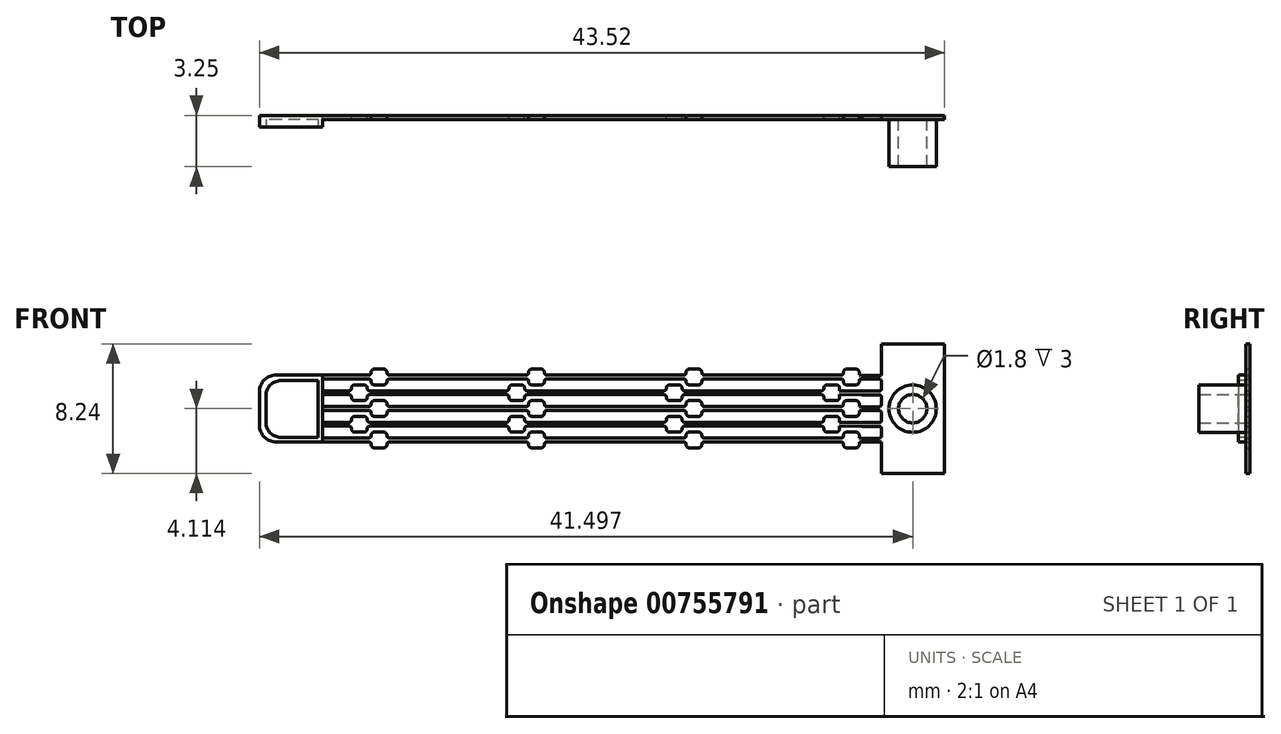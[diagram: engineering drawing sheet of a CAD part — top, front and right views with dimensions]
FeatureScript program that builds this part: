
annotation { "Feature Type Name" : "Feature", "Feature Type Description" : "" }
export const myFeature = defineFeature(function(context is Context, id is Id, definition is map)
    precondition{}
    {
        {
            var Q0;
            Q0=qCreatedBy(makeId("Front.planeOp"),FACE);
            var sketch = newSketch(context, id + "F0", { "sketchPlane" : qUnion([Q0])});
            skLineSegment(sketch, "E0.0.5.4", {"start": v(50.52, 28.02) * mm, "end": v(49.92, 28.02) * mm});
            skLineSegment(sketch, "E0.0.5.5", {"start": v(50.52, 27.02) * mm, "end": v(49.92, 27.02) * mm});
            skLineSegment(sketch, "E0.0.5.6", {"start": v(49.57, 27.4) * mm, "end": v(49.13, 27.4) * mm});
            skLineSegment(sketch, "E0.0.5.7", {"start": v(49.57, 27.64) * mm, "end": v(49.13, 27.64) * mm});
            skPoint(sketch, "E0.0.5.9", {"position": v(49.72, 27.64) * mm});
            skPoint(sketch, "E0.0.5.10", {"position": v(49.72, 28.02) * mm});
            skPoint(sketch, "E0.0.5.11", {"position": v(50.72, 27.4) * mm});
            skPoint(sketch, "E0.0.5.12", {"position": v(50.72, 28.02) * mm});
            skPoint(sketch, "E0.0.5.13", {"position": v(50.72, 27.64) * mm});
            skPoint(sketch, "E0.0.5.15", {"position": v(50.22, 27.52) * mm});
            skLineSegment(sketch, "E0.0.5.18", {"start": v(49.13, 27.4) * mm, "end": v(47.89, 27.4) * mm});
            skLineSegment(sketch, "E0.0.5.19", {"start": v(49.13, 27.64) * mm, "end": v(47.89, 27.64) * mm});
            skPoint(sketch, "E0.0.5.29", {"position": v(49.72, 27.4) * mm});
            skPoint(sketch, "E0.0.5.31", {"position": v(50.22, 27.52) * mm});
            skLineSegment(sketch, "E0.0.5.32", {"start": v(51.17, 27.4) * mm, "end": v(50.87, 27.4) * mm});
            skLineSegment(sketch, "E0.0.5.33", {"start": v(51.17, 27.64) * mm, "end": v(50.87, 27.64) * mm});
            skArc(sketch, "E0.0.5.34", {"start": v(50.72, 27.8) * mm, "mid": v(50.77, 27.69) * mm, "end": v(50.87, 27.64) * mm});
            skArc(sketch, "E0.0.5.41", {"start": v(50.52, 27.02) * mm, "mid": v(50.66, 27.08) * mm, "end": v(50.72, 27.22) * mm});
            skArc(sketch, "E0.0.5.44", {"start": v(49.72, 27.22) * mm, "mid": v(49.78, 27.08) * mm, "end": v(49.92, 27.02) * mm});
            skArc(sketch, "E0.0.5.45", {"start": v(49.92, 28.02) * mm, "mid": v(49.78, 27.96) * mm, "end": v(49.72, 27.82) * mm});
            skArc(sketch, "E0.0.5.46", {"start": v(50.72, 27.82) * mm, "mid": v(50.66, 27.96) * mm, "end": v(50.52, 28.02) * mm});
            skLineSegment(sketch, "E0.0.5.49", {"start": v(49.72, 27.22) * mm, "end": v(49.72, 27.24) * mm});
            skLineSegment(sketch, "E0.0.5.50", {"start": v(50.72, 27.22) * mm, "end": v(50.72, 27.24) * mm});
            skArc(sketch, "E0.0.5.55", {"start": v(49.72, 27.24) * mm, "mid": v(49.68, 27.35) * mm, "end": v(49.57, 27.4) * mm});
            skArc(sketch, "E0.0.5.56", {"start": v(50.87, 27.4) * mm, "mid": v(50.77, 27.35) * mm, "end": v(50.72, 27.24) * mm});
            skLineSegment(sketch, "E0.0.5.57", {"start": v(49.72, 27.8) * mm, "end": v(49.72, 27.82) * mm});
            skLineSegment(sketch, "E0.0.5.60", {"start": v(50.72, 27.8) * mm, "end": v(50.72, 27.82) * mm});
            skArc(sketch, "E0.0.5.61", {"start": v(49.57, 27.64) * mm, "mid": v(49.68, 27.69) * mm, "end": v(49.72, 27.8) * mm});
            skLineSegment(sketch, "E0.0.6.0", {"start": v(47.89, 28.4) * mm, "end": v(48.32, 28.4) * mm});
            skLineSegment(sketch, "E0.0.6.1", {"start": v(47.89, 28.64) * mm, "end": v(48.32, 28.64) * mm});
            skLineSegment(sketch, "E0.0.6.2", {"start": v(49.27, 29.02) * mm, "end": v(48.67, 29.02) * mm});
            skLineSegment(sketch, "E0.0.6.3", {"start": v(49.27, 28.02) * mm, "end": v(48.67, 28.02) * mm});
            skLineSegment(sketch, "E0.0.6.4", {"start": v(50.52, 30.02) * mm, "end": v(49.92, 30.02) * mm});
            skLineSegment(sketch, "E0.0.6.5", {"start": v(50.52, 29.02) * mm, "end": v(49.92, 29.02) * mm});
            skLineSegment(sketch, "E0.0.6.6", {"start": v(49.57, 29.4) * mm, "end": v(49.13, 29.4) * mm});
            skLineSegment(sketch, "E0.0.6.7", {"start": v(49.57, 29.64) * mm, "end": v(49.13, 29.64) * mm});
            skPoint(sketch, "E0.0.6.8", {"position": v(49.72, 29.02) * mm});
            skPoint(sketch, "E0.0.6.9", {"position": v(49.72, 29.64) * mm});
            skPoint(sketch, "E0.0.6.10", {"position": v(49.72, 30.02) * mm});
            skPoint(sketch, "E0.0.6.11", {"position": v(50.72, 29.4) * mm});
            skPoint(sketch, "E0.0.6.12", {"position": v(50.72, 30.02) * mm});
            skPoint(sketch, "E0.0.6.13", {"position": v(50.72, 29.64) * mm});
            skPoint(sketch, "E0.0.6.14", {"position": v(48.97, 28.52) * mm});
            skPoint(sketch, "E0.0.6.15", {"position": v(50.22, 29.52) * mm});
            skPoint(sketch, "E0.0.6.16", {"position": v(49.47, 28.02) * mm});
            skPoint(sketch, "E0.0.6.17", {"position": v(48.47, 28.4) * mm});
            skLineSegment(sketch, "E0.0.6.18", {"start": v(49.13, 29.4) * mm, "end": v(47.89, 29.4) * mm});
            skLineSegment(sketch, "E0.0.6.19", {"start": v(49.13, 29.64) * mm, "end": v(47.89, 29.64) * mm});
            skPoint(sketch, "E0.0.6.20", {"position": v(48.47, 28.02) * mm});
            skPoint(sketch, "E0.0.6.21", {"position": v(48.47, 28.64) * mm});
            skLineSegment(sketch, "E0.0.6.22", {"start": v(49.62, 28.4) * mm, "end": v(51.17, 28.4) * mm});
            skPoint(sketch, "E0.0.6.23", {"position": v(48.47, 29.02) * mm});
            skPoint(sketch, "E0.0.6.24", {"position": v(49.47, 28.4) * mm});
            skLineSegment(sketch, "E0.0.6.25", {"start": v(49.62, 28.64) * mm, "end": v(51.17, 28.64) * mm});
            skPoint(sketch, "E0.0.6.26", {"position": v(49.47, 29.02) * mm});
            skPoint(sketch, "E0.0.6.27", {"position": v(49.47, 28.64) * mm});
            skPoint(sketch, "E0.0.6.28", {"position": v(50.72, 29.02) * mm});
            skPoint(sketch, "E0.0.6.29", {"position": v(49.72, 29.4) * mm});
            skPoint(sketch, "E0.0.6.30", {"position": v(48.97, 28.52) * mm});
            skPoint(sketch, "E0.0.6.31", {"position": v(50.22, 29.52) * mm});
            skLineSegment(sketch, "E0.0.6.32", {"start": v(51.17, 29.4) * mm, "end": v(50.87, 29.4) * mm});
            skLineSegment(sketch, "E0.0.6.33", {"start": v(51.17, 29.64) * mm, "end": v(50.87, 29.64) * mm});
            skArc(sketch, "E0.0.6.34", {"start": v(50.72, 29.8) * mm, "mid": v(50.77, 29.69) * mm, "end": v(50.87, 29.64) * mm});
            skArc(sketch, "E0.0.6.35", {"start": v(49.27, 28.02) * mm, "mid": v(49.41, 28.08) * mm, "end": v(49.47, 28.22) * mm});
            skArc(sketch, "E0.0.6.36", {"start": v(48.47, 28.22) * mm, "mid": v(48.53, 28.08) * mm, "end": v(48.67, 28.02) * mm});
            skArc(sketch, "E0.0.6.37", {"start": v(48.67, 29.02) * mm, "mid": v(48.53, 28.96) * mm, "end": v(48.47, 28.82) * mm});
            skArc(sketch, "E0.0.6.39", {"start": v(49.47, 28.82) * mm, "mid": v(49.41, 28.96) * mm, "end": v(49.27, 29.02) * mm});
            skArc(sketch, "E0.0.6.41", {"start": v(50.52, 29.02) * mm, "mid": v(50.66, 29.08) * mm, "end": v(50.72, 29.22) * mm});
            skArc(sketch, "E0.0.6.44", {"start": v(49.72, 29.22) * mm, "mid": v(49.78, 29.08) * mm, "end": v(49.92, 29.02) * mm});
            skArc(sketch, "E0.0.6.45", {"start": v(49.92, 30.02) * mm, "mid": v(49.78, 29.96) * mm, "end": v(49.72, 29.82) * mm});
            skArc(sketch, "E0.0.6.46", {"start": v(50.72, 29.82) * mm, "mid": v(50.66, 29.96) * mm, "end": v(50.52, 30.02) * mm});
            skArc(sketch, "E0.0.6.47", {"start": v(48.47, 28.24) * mm, "mid": v(48.43, 28.35) * mm, "end": v(48.32, 28.4) * mm});
            skArc(sketch, "E0.0.6.48", {"start": v(49.62, 28.4) * mm, "mid": v(49.52, 28.35) * mm, "end": v(49.47, 28.24) * mm});
            skLineSegment(sketch, "E0.0.6.49", {"start": v(49.72, 29.22) * mm, "end": v(49.72, 29.24) * mm});
            skLineSegment(sketch, "E0.0.6.50", {"start": v(50.72, 29.22) * mm, "end": v(50.72, 29.24) * mm});
            skArc(sketch, "E0.0.6.51", {"start": v(48.32, 28.64) * mm, "mid": v(48.43, 28.69) * mm, "end": v(48.47, 28.8) * mm});
            skLineSegment(sketch, "E0.0.6.52", {"start": v(48.47, 28.8) * mm, "end": v(48.47, 28.82) * mm});
            skArc(sketch, "E0.0.6.53", {"start": v(49.47, 28.8) * mm, "mid": v(49.52, 28.69) * mm, "end": v(49.62, 28.64) * mm});
            skLineSegment(sketch, "E0.0.6.54", {"start": v(49.47, 28.8) * mm, "end": v(49.47, 28.82) * mm});
            skArc(sketch, "E0.0.6.55", {"start": v(49.72, 29.24) * mm, "mid": v(49.68, 29.35) * mm, "end": v(49.57, 29.4) * mm});
            skArc(sketch, "E0.0.6.56", {"start": v(50.87, 29.4) * mm, "mid": v(50.77, 29.35) * mm, "end": v(50.72, 29.24) * mm});
            skLineSegment(sketch, "E0.0.6.57", {"start": v(49.72, 29.8) * mm, "end": v(49.72, 29.82) * mm});
            skLineSegment(sketch, "E0.0.6.58", {"start": v(48.47, 28.22) * mm, "end": v(48.47, 28.24) * mm});
            skLineSegment(sketch, "E0.0.6.59", {"start": v(49.47, 28.22) * mm, "end": v(49.47, 28.24) * mm});
            skLineSegment(sketch, "E0.0.6.60", {"start": v(50.72, 29.8) * mm, "end": v(50.72, 29.82) * mm});
            skArc(sketch, "E0.0.6.61", {"start": v(49.57, 29.64) * mm, "mid": v(49.68, 29.69) * mm, "end": v(49.72, 29.8) * mm});
            skLineSegment(sketch, "E0.0.7.0", {"start": v(47.89, 30.4) * mm, "end": v(48.32, 30.4) * mm});
            skLineSegment(sketch, "E0.0.7.1", {"start": v(47.89, 30.64) * mm, "end": v(48.32, 30.64) * mm});
            skLineSegment(sketch, "E0.0.7.2", {"start": v(49.27, 31.02) * mm, "end": v(48.67, 31.02) * mm});
            skLineSegment(sketch, "E0.0.7.3", {"start": v(49.27, 30.02) * mm, "end": v(48.67, 30.02) * mm});
            skLineSegment(sketch, "E0.0.7.4", {"start": v(50.52, 32.02) * mm, "end": v(49.92, 32.02) * mm});
            skLineSegment(sketch, "E0.0.7.5", {"start": v(50.52, 31.02) * mm, "end": v(49.92, 31.02) * mm});
            skLineSegment(sketch, "E0.0.7.6", {"start": v(49.57, 31.4) * mm, "end": v(49.13, 31.4) * mm});
            skLineSegment(sketch, "E0.0.7.7", {"start": v(49.57, 31.64) * mm, "end": v(49.13, 31.64) * mm});
            skPoint(sketch, "E0.0.7.8", {"position": v(49.72, 31.02) * mm});
            skPoint(sketch, "E0.0.7.9", {"position": v(49.72, 31.64) * mm});
            skPoint(sketch, "E0.0.7.10", {"position": v(49.72, 32.02) * mm});
            skPoint(sketch, "E0.0.7.11", {"position": v(50.72, 31.4) * mm});
            skPoint(sketch, "E0.0.7.12", {"position": v(50.72, 32.02) * mm});
            skPoint(sketch, "E0.0.7.13", {"position": v(50.72, 31.64) * mm});
            skPoint(sketch, "E0.0.7.14", {"position": v(48.97, 30.52) * mm});
            skPoint(sketch, "E0.0.7.15", {"position": v(50.22, 31.52) * mm});
            skPoint(sketch, "E0.0.7.16", {"position": v(49.47, 30.02) * mm});
            skPoint(sketch, "E0.0.7.17", {"position": v(48.47, 30.4) * mm});
            skLineSegment(sketch, "E0.0.7.18", {"start": v(49.13, 31.4) * mm, "end": v(47.89, 31.4) * mm});
            skLineSegment(sketch, "E0.0.7.19", {"start": v(49.13, 31.64) * mm, "end": v(47.89, 31.64) * mm});
            skPoint(sketch, "E0.0.7.20", {"position": v(48.47, 30.02) * mm});
            skPoint(sketch, "E0.0.7.21", {"position": v(48.47, 30.64) * mm});
            skLineSegment(sketch, "E0.0.7.22", {"start": v(49.62, 30.4) * mm, "end": v(51.17, 30.4) * mm});
            skPoint(sketch, "E0.0.7.23", {"position": v(48.47, 31.02) * mm});
            skPoint(sketch, "E0.0.7.24", {"position": v(49.47, 30.4) * mm});
            skLineSegment(sketch, "E0.0.7.25", {"start": v(49.62, 30.64) * mm, "end": v(51.17, 30.64) * mm});
            skPoint(sketch, "E0.0.7.26", {"position": v(49.47, 31.02) * mm});
            skPoint(sketch, "E0.0.7.27", {"position": v(49.47, 30.64) * mm});
            skPoint(sketch, "E0.0.7.28", {"position": v(50.72, 31.02) * mm});
            skPoint(sketch, "E0.0.7.29", {"position": v(49.72, 31.4) * mm});
            skPoint(sketch, "E0.0.7.30", {"position": v(48.97, 30.52) * mm});
            skPoint(sketch, "E0.0.7.31", {"position": v(50.22, 31.52) * mm});
            skLineSegment(sketch, "E0.0.7.32", {"start": v(51.17, 31.4) * mm, "end": v(50.87, 31.4) * mm});
            skLineSegment(sketch, "E0.0.7.33", {"start": v(51.17, 31.64) * mm, "end": v(50.87, 31.64) * mm});
            skArc(sketch, "E0.0.7.34", {"start": v(50.72, 31.8) * mm, "mid": v(50.77, 31.69) * mm, "end": v(50.87, 31.64) * mm});
            skArc(sketch, "E0.0.7.35", {"start": v(49.27, 30.02) * mm, "mid": v(49.41, 30.08) * mm, "end": v(49.47, 30.22) * mm});
            skArc(sketch, "E0.0.7.36", {"start": v(48.47, 30.22) * mm, "mid": v(48.53, 30.08) * mm, "end": v(48.67, 30.02) * mm});
            skArc(sketch, "E0.0.7.37", {"start": v(48.67, 31.02) * mm, "mid": v(48.53, 30.96) * mm, "end": v(48.47, 30.82) * mm});
            skArc(sketch, "E0.0.7.39", {"start": v(49.47, 30.82) * mm, "mid": v(49.41, 30.96) * mm, "end": v(49.27, 31.02) * mm});
            skArc(sketch, "E0.0.7.41", {"start": v(50.52, 31.02) * mm, "mid": v(50.66, 31.08) * mm, "end": v(50.72, 31.22) * mm});
            skArc(sketch, "E0.0.7.44", {"start": v(49.72, 31.22) * mm, "mid": v(49.78, 31.08) * mm, "end": v(49.92, 31.02) * mm});
            skArc(sketch, "E0.0.7.45", {"start": v(49.92, 32.02) * mm, "mid": v(49.78, 31.96) * mm, "end": v(49.72, 31.82) * mm});
            skArc(sketch, "E0.0.7.46", {"start": v(50.72, 31.82) * mm, "mid": v(50.66, 31.96) * mm, "end": v(50.52, 32.02) * mm});
            skArc(sketch, "E0.0.7.47", {"start": v(48.47, 30.24) * mm, "mid": v(48.43, 30.35) * mm, "end": v(48.32, 30.4) * mm});
            skArc(sketch, "E0.0.7.48", {"start": v(49.62, 30.4) * mm, "mid": v(49.52, 30.35) * mm, "end": v(49.47, 30.24) * mm});
            skLineSegment(sketch, "E0.0.7.49", {"start": v(49.72, 31.22) * mm, "end": v(49.72, 31.24) * mm});
            skLineSegment(sketch, "E0.0.7.50", {"start": v(50.72, 31.22) * mm, "end": v(50.72, 31.24) * mm});
            skArc(sketch, "E0.0.7.51", {"start": v(48.32, 30.64) * mm, "mid": v(48.43, 30.69) * mm, "end": v(48.47, 30.8) * mm});
            skLineSegment(sketch, "E0.0.7.52", {"start": v(48.47, 30.8) * mm, "end": v(48.47, 30.82) * mm});
            skArc(sketch, "E0.0.7.53", {"start": v(49.47, 30.8) * mm, "mid": v(49.52, 30.69) * mm, "end": v(49.62, 30.64) * mm});
            skLineSegment(sketch, "E0.0.7.54", {"start": v(49.47, 30.8) * mm, "end": v(49.47, 30.82) * mm});
            skArc(sketch, "E0.0.7.55", {"start": v(49.72, 31.24) * mm, "mid": v(49.68, 31.35) * mm, "end": v(49.57, 31.4) * mm});
            skArc(sketch, "E0.0.7.56", {"start": v(50.87, 31.4) * mm, "mid": v(50.77, 31.35) * mm, "end": v(50.72, 31.24) * mm});
            skLineSegment(sketch, "E0.0.7.57", {"start": v(49.72, 31.8) * mm, "end": v(49.72, 31.82) * mm});
            skLineSegment(sketch, "E0.0.7.58", {"start": v(48.47, 30.22) * mm, "end": v(48.47, 30.24) * mm});
            skLineSegment(sketch, "E0.0.7.59", {"start": v(49.47, 30.22) * mm, "end": v(49.47, 30.24) * mm});
            skLineSegment(sketch, "E0.0.7.60", {"start": v(50.72, 31.8) * mm, "end": v(50.72, 31.82) * mm});
            skArc(sketch, "E0.0.7.61", {"start": v(49.57, 31.64) * mm, "mid": v(49.68, 31.69) * mm, "end": v(49.72, 31.8) * mm});
            skPoint(sketch, "E1.1.0.2", {"position": v(59.72, 32.02) * mm});
            skPoint(sketch, "E1.1.0.3", {"position": v(60.72, 32.02) * mm});
            skPoint(sketch, "E1.1.0.6", {"position": v(60.72, 31.64) * mm});
            skPoint(sketch, "E1.1.0.8", {"position": v(58.47, 28.02) * mm});
            skPoint(sketch, "E1.1.0.11", {"position": v(60.22, 31.52) * mm});
            skPoint(sketch, "E1.1.0.14", {"position": v(59.47, 30.02) * mm});
            skPoint(sketch, "E1.1.0.15", {"position": v(58.47, 29.02) * mm});
            skPoint(sketch, "E1.1.0.17", {"position": v(59.72, 28.02) * mm});
            skPoint(sketch, "E1.1.0.20", {"position": v(58.47, 30.02) * mm});
            skPoint(sketch, "E1.1.0.21", {"position": v(60.72, 27.4) * mm});
            skPoint(sketch, "E1.1.0.22", {"position": v(58.47, 30.64) * mm});
            skPoint(sketch, "E1.1.0.32", {"position": v(60.72, 29.02) * mm});
            skPoint(sketch, "E1.1.0.33", {"position": v(58.47, 31.02) * mm});
            skPoint(sketch, "E1.1.0.34", {"position": v(60.72, 28.02) * mm});
            skPoint(sketch, "E1.1.0.35", {"position": v(59.72, 29.02) * mm});
            skPoint(sketch, "E1.1.0.38", {"position": v(59.72, 31.64) * mm});
            skPoint(sketch, "E1.1.0.39", {"position": v(60.72, 29.64) * mm});
            skPoint(sketch, "E1.1.0.43", {"position": v(60.22, 31.52) * mm});
            skPoint(sketch, "E1.1.0.44", {"position": v(60.72, 31.4) * mm});
            skPoint(sketch, "E1.1.0.49", {"position": v(58.47, 28.4) * mm});
            skPoint(sketch, "E1.1.0.52", {"position": v(58.97, 30.52) * mm});
            skPoint(sketch, "E1.1.0.57", {"position": v(58.47, 28.64) * mm});
            skPoint(sketch, "E1.1.0.67", {"position": v(59.72, 27.64) * mm});
            skPoint(sketch, "E1.1.0.68", {"position": v(58.47, 30.4) * mm});
            skPoint(sketch, "E1.1.0.69", {"position": v(59.47, 28.4) * mm});
            skPoint(sketch, "E1.1.0.71", {"position": v(60.22, 27.52) * mm});
            skPoint(sketch, "E1.1.0.72", {"position": v(59.47, 28.64) * mm});
            skPoint(sketch, "E1.1.0.78", {"position": v(59.72, 31.4) * mm});
            skPoint(sketch, "E1.1.0.80", {"position": v(60.72, 30.02) * mm});
            skPoint(sketch, "E1.1.0.82", {"position": v(60.22, 27.52) * mm});
            skPoint(sketch, "E1.1.0.83", {"position": v(60.72, 29.4) * mm});
            skPoint(sketch, "E1.1.0.85", {"position": v(60.72, 31.02) * mm});
            skPoint(sketch, "E1.1.0.88", {"position": v(58.97, 28.52) * mm});
            skPoint(sketch, "E1.1.0.90", {"position": v(58.97, 30.52) * mm});
            skPoint(sketch, "E1.1.0.92", {"position": v(60.22, 29.52) * mm});
            skPoint(sketch, "E1.1.0.94", {"position": v(60.72, 27.64) * mm});
            skPoint(sketch, "E1.1.0.106", {"position": v(59.72, 27.4) * mm});
            skPoint(sketch, "E1.1.0.110", {"position": v(59.47, 29.02) * mm});
            skPoint(sketch, "E1.1.0.113", {"position": v(60.22, 29.52) * mm});
            skPoint(sketch, "E1.1.0.117", {"position": v(59.72, 31.02) * mm});
            skPoint(sketch, "E1.1.0.126", {"position": v(59.47, 28.02) * mm});
            skPoint(sketch, "E1.1.0.134", {"position": v(58.97, 28.52) * mm});
            skPoint(sketch, "E1.1.0.141", {"position": v(59.47, 30.64) * mm});
            skPoint(sketch, "E1.1.0.147", {"position": v(59.72, 30.02) * mm});
            skPoint(sketch, "E1.1.0.148", {"position": v(59.47, 31.02) * mm});
            skPoint(sketch, "E1.1.0.154", {"position": v(59.47, 30.4) * mm});
            skPoint(sketch, "E1.1.0.155", {"position": v(59.72, 29.4) * mm});
            skPoint(sketch, "E1.1.0.156", {"position": v(59.72, 29.64) * mm});
            skLineSegment(sketch, "E1.1.0.161", {"start": v(59.13, 31.64) * mm, "end": v(57.89, 31.64) * mm});
            skLineSegment(sketch, "E1.1.0.162", {"start": v(59.13, 31.4) * mm, "end": v(57.89, 31.4) * mm});
            skLineSegment(sketch, "E1.1.0.163", {"start": v(57.89, 30.64) * mm, "end": v(58.32, 30.64) * mm});
            skLineSegment(sketch, "E1.1.0.166", {"start": v(57.89, 30.4) * mm, "end": v(58.32, 30.4) * mm});
            skLineSegment(sketch, "E1.1.0.171", {"start": v(59.13, 29.64) * mm, "end": v(57.89, 29.64) * mm});
            skLineSegment(sketch, "E1.1.0.173", {"start": v(59.13, 29.4) * mm, "end": v(57.89, 29.4) * mm});
            skLineSegment(sketch, "E1.1.0.174", {"start": v(59.13, 27.64) * mm, "end": v(57.89, 27.64) * mm});
            skArc(sketch, "E1.1.0.175", {"start": v(58.47, 28.22) * mm, "mid": v(58.53, 28.08) * mm, "end": v(58.67, 28.02) * mm});
            skLineSegment(sketch, "E1.1.0.176", {"start": v(57.89, 28.4) * mm, "end": v(58.32, 28.4) * mm});
            skLineSegment(sketch, "E1.1.0.177", {"start": v(57.89, 28.64) * mm, "end": v(58.32, 28.64) * mm});
            skLineSegment(sketch, "E1.1.0.180", {"start": v(60.52, 32.02) * mm, "end": v(59.92, 32.02) * mm});
            skLineSegment(sketch, "E1.1.0.185", {"start": v(61.17, 31.64) * mm, "end": v(60.87, 31.64) * mm});
            skLineSegment(sketch, "E1.1.0.194", {"start": v(59.13, 27.4) * mm, "end": v(57.89, 27.4) * mm});
            skLineSegment(sketch, "E1.1.0.205", {"start": v(61.17, 31.4) * mm, "end": v(60.87, 31.4) * mm});
            skArc(sketch, "E1.1.0.215", {"start": v(59.57, 31.64) * mm, "mid": v(59.68, 31.69) * mm, "end": v(59.72, 31.8) * mm});
            skArc(sketch, "E1.1.0.216", {"start": v(60.72, 31.82) * mm, "mid": v(60.66, 31.96) * mm, "end": v(60.52, 32.02) * mm});
            skArc(sketch, "E1.1.0.218", {"start": v(60.72, 31.8) * mm, "mid": v(60.77, 31.69) * mm, "end": v(60.87, 31.64) * mm});
            skLineSegment(sketch, "E1.1.0.222", {"start": v(61.17, 29.64) * mm, "end": v(60.87, 29.64) * mm});
            skLineSegment(sketch, "E1.1.0.228", {"start": v(59.72, 31.8) * mm, "end": v(59.72, 31.82) * mm});
            skLineSegment(sketch, "E1.1.0.229", {"start": v(60.72, 31.8) * mm, "end": v(60.72, 31.82) * mm});
            skLineSegment(sketch, "E1.1.0.230", {"start": v(59.62, 30.64) * mm, "end": v(61.17, 30.64) * mm});
            skArc(sketch, "E1.1.0.231", {"start": v(59.92, 32.02) * mm, "mid": v(59.78, 31.96) * mm, "end": v(59.72, 31.82) * mm});
            skLineSegment(sketch, "E1.1.0.239", {"start": v(59.27, 31.02) * mm, "end": v(58.67, 31.02) * mm});
            skLineSegment(sketch, "E1.1.0.240", {"start": v(61.17, 29.4) * mm, "end": v(60.87, 29.4) * mm});
            skLineSegment(sketch, "E1.1.0.242", {"start": v(59.57, 31.64) * mm, "end": v(59.13, 31.64) * mm});
            skArc(sketch, "E1.1.0.243", {"start": v(59.47, 30.82) * mm, "mid": v(59.41, 30.96) * mm, "end": v(59.27, 31.02) * mm});
            skArc(sketch, "E1.1.0.244", {"start": v(59.72, 31.24) * mm, "mid": v(59.68, 31.35) * mm, "end": v(59.57, 31.4) * mm});
            skArc(sketch, "E1.1.0.246", {"start": v(60.87, 31.4) * mm, "mid": v(60.77, 31.35) * mm, "end": v(60.72, 31.24) * mm});
            skLineSegment(sketch, "E1.1.0.249", {"start": v(59.57, 31.4) * mm, "end": v(59.13, 31.4) * mm});
            skLineSegment(sketch, "E1.1.0.250", {"start": v(60.52, 31.02) * mm, "end": v(59.92, 31.02) * mm});
            skArc(sketch, "E1.1.0.251", {"start": v(60.52, 31.02) * mm, "mid": v(60.66, 31.08) * mm, "end": v(60.72, 31.22) * mm});
            skLineSegment(sketch, "E1.1.0.253", {"start": v(59.62, 30.4) * mm, "end": v(61.17, 30.4) * mm});
            skLineSegment(sketch, "E1.1.0.257", {"start": v(59.72, 31.22) * mm, "end": v(59.72, 31.24) * mm});
            skLineSegment(sketch, "E1.1.0.259", {"start": v(60.72, 31.22) * mm, "end": v(60.72, 31.24) * mm});
            skArc(sketch, "E1.1.0.260", {"start": v(58.32, 30.64) * mm, "mid": v(58.43, 30.69) * mm, "end": v(58.47, 30.8) * mm});
            skArc(sketch, "E1.1.0.264", {"start": v(58.67, 31.02) * mm, "mid": v(58.53, 30.96) * mm, "end": v(58.47, 30.82) * mm});
            skLineSegment(sketch, "E1.1.0.265", {"start": v(59.62, 28.64) * mm, "end": v(61.17, 28.64) * mm});
            skArc(sketch, "E1.1.0.266", {"start": v(59.47, 30.8) * mm, "mid": v(59.52, 30.69) * mm, "end": v(59.62, 30.64) * mm});
            skLineSegment(sketch, "E1.1.0.269", {"start": v(59.47, 30.8) * mm, "end": v(59.47, 30.82) * mm});
            skLineSegment(sketch, "E1.1.0.274", {"start": v(61.17, 27.4) * mm, "end": v(60.87, 27.4) * mm});
            skArc(sketch, "E1.1.0.275", {"start": v(58.47, 30.24) * mm, "mid": v(58.43, 30.35) * mm, "end": v(58.32, 30.4) * mm});
            skLineSegment(sketch, "E1.1.0.276", {"start": v(61.17, 27.64) * mm, "end": v(60.87, 27.64) * mm});
            skArc(sketch, "E1.1.0.278", {"start": v(59.72, 31.22) * mm, "mid": v(59.78, 31.08) * mm, "end": v(59.92, 31.02) * mm});
            skArc(sketch, "E1.1.0.280", {"start": v(59.62, 30.4) * mm, "mid": v(59.52, 30.35) * mm, "end": v(59.47, 30.24) * mm});
            skLineSegment(sketch, "E1.1.0.284", {"start": v(59.62, 28.4) * mm, "end": v(61.17, 28.4) * mm});
            skLineSegment(sketch, "E1.1.0.285", {"start": v(58.47, 30.8) * mm, "end": v(58.47, 30.82) * mm});
            skLineSegment(sketch, "E1.1.0.288", {"start": v(60.52, 29.02) * mm, "end": v(59.92, 29.02) * mm});
            skArc(sketch, "E1.1.0.289", {"start": v(59.47, 28.82) * mm, "mid": v(59.41, 28.96) * mm, "end": v(59.27, 29.02) * mm});
            skLineSegment(sketch, "E1.1.0.290", {"start": v(60.52, 30.02) * mm, "end": v(59.92, 30.02) * mm});
            skLineSegment(sketch, "E1.1.0.292", {"start": v(59.27, 29.02) * mm, "end": v(58.67, 29.02) * mm});
            skLineSegment(sketch, "E1.1.0.293", {"start": v(59.27, 28.02) * mm, "end": v(58.67, 28.02) * mm});
            skLineSegment(sketch, "E1.1.0.295", {"start": v(59.57, 29.64) * mm, "end": v(59.13, 29.64) * mm});
            skArc(sketch, "E1.1.0.298", {"start": v(59.92, 30.02) * mm, "mid": v(59.78, 29.96) * mm, "end": v(59.72, 29.82) * mm});
            skArc(sketch, "E1.1.0.299", {"start": v(59.57, 29.64) * mm, "mid": v(59.68, 29.69) * mm, "end": v(59.72, 29.8) * mm});
            skArc(sketch, "E1.1.0.301", {"start": v(60.72, 29.82) * mm, "mid": v(60.66, 29.96) * mm, "end": v(60.52, 30.02) * mm});
            skArc(sketch, "E1.1.0.304", {"start": v(58.47, 28.24) * mm, "mid": v(58.43, 28.35) * mm, "end": v(58.32, 28.4) * mm});
            skArc(sketch, "E1.1.0.305", {"start": v(58.67, 29.02) * mm, "mid": v(58.53, 28.96) * mm, "end": v(58.47, 28.82) * mm});
            skArc(sketch, "E1.1.0.308", {"start": v(59.62, 28.4) * mm, "mid": v(59.52, 28.35) * mm, "end": v(59.47, 28.24) * mm});
            skLineSegment(sketch, "E1.1.0.311", {"start": v(59.27, 30.02) * mm, "end": v(58.67, 30.02) * mm});
            skLineSegment(sketch, "E1.1.0.312", {"start": v(59.72, 29.22) * mm, "end": v(59.72, 29.24) * mm});
            skLineSegment(sketch, "E1.1.0.315", {"start": v(60.72, 29.22) * mm, "end": v(60.72, 29.24) * mm});
            skArc(sketch, "E1.1.0.316", {"start": v(60.72, 29.8) * mm, "mid": v(60.77, 29.69) * mm, "end": v(60.87, 29.64) * mm});
            skArc(sketch, "E1.1.0.317", {"start": v(59.92, 28.02) * mm, "mid": v(59.78, 27.96) * mm, "end": v(59.72, 27.82) * mm});
            skLineSegment(sketch, "E1.1.0.326", {"start": v(58.47, 30.22) * mm, "end": v(58.47, 30.24) * mm});
            skLineSegment(sketch, "E1.1.0.327", {"start": v(58.47, 28.8) * mm, "end": v(58.47, 28.82) * mm});
            skArc(sketch, "E1.1.0.328", {"start": v(60.72, 27.82) * mm, "mid": v(60.66, 27.96) * mm, "end": v(60.52, 28.02) * mm});
            skArc(sketch, "E1.1.0.333", {"start": v(59.27, 28.02) * mm, "mid": v(59.41, 28.08) * mm, "end": v(59.47, 28.22) * mm});
            skArc(sketch, "E1.1.0.337", {"start": v(60.52, 29.02) * mm, "mid": v(60.66, 29.08) * mm, "end": v(60.72, 29.22) * mm});
            skLineSegment(sketch, "E1.1.0.340", {"start": v(59.72, 29.8) * mm, "end": v(59.72, 29.82) * mm});
            skLineSegment(sketch, "E1.1.0.343", {"start": v(59.57, 29.4) * mm, "end": v(59.13, 29.4) * mm});
            skLineSegment(sketch, "E1.1.0.345", {"start": v(58.47, 28.22) * mm, "end": v(58.47, 28.24) * mm});
            skLineSegment(sketch, "E1.1.0.349", {"start": v(59.47, 28.22) * mm, "end": v(59.47, 28.24) * mm});
            skArc(sketch, "E1.1.0.356", {"start": v(59.72, 29.22) * mm, "mid": v(59.78, 29.08) * mm, "end": v(59.92, 29.02) * mm});
            skLineSegment(sketch, "E1.1.0.357", {"start": v(60.72, 29.8) * mm, "end": v(60.72, 29.82) * mm});
            skArc(sketch, "E1.1.0.363", {"start": v(59.27, 30.02) * mm, "mid": v(59.41, 30.08) * mm, "end": v(59.47, 30.22) * mm});
            skLineSegment(sketch, "E1.1.0.369", {"start": v(60.52, 28.02) * mm, "end": v(59.92, 28.02) * mm});
            skArc(sketch, "E1.1.0.371", {"start": v(58.47, 30.22) * mm, "mid": v(58.53, 30.08) * mm, "end": v(58.67, 30.02) * mm});
            skArc(sketch, "E1.1.0.374", {"start": v(60.52, 27.02) * mm, "mid": v(60.66, 27.08) * mm, "end": v(60.72, 27.22) * mm});
            skLineSegment(sketch, "E1.1.0.375", {"start": v(60.52, 27.02) * mm, "end": v(59.92, 27.02) * mm});
            skLineSegment(sketch, "E1.1.0.377", {"start": v(59.57, 27.4) * mm, "end": v(59.13, 27.4) * mm});
            skLineSegment(sketch, "E1.1.0.382", {"start": v(59.57, 27.64) * mm, "end": v(59.13, 27.64) * mm});
            skArc(sketch, "E1.1.0.383", {"start": v(59.47, 28.8) * mm, "mid": v(59.52, 28.69) * mm, "end": v(59.62, 28.64) * mm});
            skLineSegment(sketch, "E1.1.0.385", {"start": v(60.72, 27.8) * mm, "end": v(60.72, 27.82) * mm});
            skArc(sketch, "E1.1.0.386", {"start": v(59.72, 27.22) * mm, "mid": v(59.78, 27.08) * mm, "end": v(59.92, 27.02) * mm});
            skArc(sketch, "E1.1.0.390", {"start": v(59.57, 27.64) * mm, "mid": v(59.68, 27.69) * mm, "end": v(59.72, 27.8) * mm});
            skArc(sketch, "E1.1.0.397", {"start": v(58.32, 28.64) * mm, "mid": v(58.43, 28.69) * mm, "end": v(58.47, 28.8) * mm});
            skArc(sketch, "E1.1.0.399", {"start": v(60.72, 27.8) * mm, "mid": v(60.77, 27.69) * mm, "end": v(60.87, 27.64) * mm});
            skLineSegment(sketch, "E1.1.0.402", {"start": v(59.47, 28.8) * mm, "end": v(59.47, 28.82) * mm});
            skArc(sketch, "E1.1.0.403", {"start": v(60.87, 29.4) * mm, "mid": v(60.77, 29.35) * mm, "end": v(60.72, 29.24) * mm});
            skArc(sketch, "E1.1.0.410", {"start": v(59.72, 29.24) * mm, "mid": v(59.68, 29.35) * mm, "end": v(59.57, 29.4) * mm});
            skArc(sketch, "E1.1.0.418", {"start": v(59.72, 27.24) * mm, "mid": v(59.68, 27.35) * mm, "end": v(59.57, 27.4) * mm});
            skArc(sketch, "E1.1.0.421", {"start": v(60.87, 27.4) * mm, "mid": v(60.77, 27.35) * mm, "end": v(60.72, 27.24) * mm});
            skLineSegment(sketch, "E1.1.0.423", {"start": v(59.72, 27.8) * mm, "end": v(59.72, 27.82) * mm});
            skLineSegment(sketch, "E1.1.0.426", {"start": v(59.47, 30.22) * mm, "end": v(59.47, 30.24) * mm});
            skLineSegment(sketch, "E1.1.0.430", {"start": v(59.72, 27.22) * mm, "end": v(59.72, 27.24) * mm});
            skLineSegment(sketch, "E1.1.0.432", {"start": v(60.72, 27.22) * mm, "end": v(60.72, 27.24) * mm});
            skPoint(sketch, "E1.2.0.2", {"position": v(69.72, 32.02) * mm});
            skPoint(sketch, "E1.2.0.3", {"position": v(70.72, 32.02) * mm});
            skPoint(sketch, "E1.2.0.6", {"position": v(70.72, 31.64) * mm});
            skPoint(sketch, "E1.2.0.8", {"position": v(68.47, 28.02) * mm});
            skPoint(sketch, "E1.2.0.11", {"position": v(70.22, 31.52) * mm});
            skPoint(sketch, "E1.2.0.14", {"position": v(69.47, 30.02) * mm});
            skPoint(sketch, "E1.2.0.15", {"position": v(68.47, 29.02) * mm});
            skPoint(sketch, "E1.2.0.17", {"position": v(69.72, 28.02) * mm});
            skPoint(sketch, "E1.2.0.20", {"position": v(68.47, 30.02) * mm});
            skPoint(sketch, "E1.2.0.21", {"position": v(70.72, 27.4) * mm});
            skPoint(sketch, "E1.2.0.22", {"position": v(68.47, 30.64) * mm});
            skPoint(sketch, "E1.2.0.32", {"position": v(70.72, 29.02) * mm});
            skPoint(sketch, "E1.2.0.33", {"position": v(68.47, 31.02) * mm});
            skPoint(sketch, "E1.2.0.34", {"position": v(70.72, 28.02) * mm});
            skPoint(sketch, "E1.2.0.35", {"position": v(69.72, 29.02) * mm});
            skPoint(sketch, "E1.2.0.38", {"position": v(69.72, 31.64) * mm});
            skPoint(sketch, "E1.2.0.39", {"position": v(70.72, 29.64) * mm});
            skPoint(sketch, "E1.2.0.43", {"position": v(70.22, 31.52) * mm});
            skPoint(sketch, "E1.2.0.44", {"position": v(70.72, 31.4) * mm});
            skPoint(sketch, "E1.2.0.49", {"position": v(68.47, 28.4) * mm});
            skPoint(sketch, "E1.2.0.52", {"position": v(68.97, 30.52) * mm});
            skPoint(sketch, "E1.2.0.57", {"position": v(68.47, 28.64) * mm});
            skPoint(sketch, "E1.2.0.67", {"position": v(69.72, 27.64) * mm});
            skPoint(sketch, "E1.2.0.68", {"position": v(68.47, 30.4) * mm});
            skPoint(sketch, "E1.2.0.69", {"position": v(69.47, 28.4) * mm});
            skPoint(sketch, "E1.2.0.71", {"position": v(70.22, 27.52) * mm});
            skPoint(sketch, "E1.2.0.72", {"position": v(69.47, 28.64) * mm});
            skPoint(sketch, "E1.2.0.78", {"position": v(69.72, 31.4) * mm});
            skPoint(sketch, "E1.2.0.80", {"position": v(70.72, 30.02) * mm});
            skPoint(sketch, "E1.2.0.82", {"position": v(70.22, 27.52) * mm});
            skPoint(sketch, "E1.2.0.83", {"position": v(70.72, 29.4) * mm});
            skPoint(sketch, "E1.2.0.85", {"position": v(70.72, 31.02) * mm});
            skPoint(sketch, "E1.2.0.88", {"position": v(68.97, 28.52) * mm});
            skPoint(sketch, "E1.2.0.90", {"position": v(68.97, 30.52) * mm});
            skPoint(sketch, "E1.2.0.92", {"position": v(70.22, 29.52) * mm});
            skPoint(sketch, "E1.2.0.94", {"position": v(70.72, 27.64) * mm});
            skPoint(sketch, "E1.2.0.106", {"position": v(69.72, 27.4) * mm});
            skPoint(sketch, "E1.2.0.110", {"position": v(69.47, 29.02) * mm});
            skPoint(sketch, "E1.2.0.113", {"position": v(70.22, 29.52) * mm});
            skPoint(sketch, "E1.2.0.117", {"position": v(69.72, 31.02) * mm});
            skPoint(sketch, "E1.2.0.126", {"position": v(69.47, 28.02) * mm});
            skPoint(sketch, "E1.2.0.134", {"position": v(68.97, 28.52) * mm});
            skPoint(sketch, "E1.2.0.141", {"position": v(69.47, 30.64) * mm});
            skPoint(sketch, "E1.2.0.147", {"position": v(69.72, 30.02) * mm});
            skPoint(sketch, "E1.2.0.148", {"position": v(69.47, 31.02) * mm});
            skPoint(sketch, "E1.2.0.154", {"position": v(69.47, 30.4) * mm});
            skPoint(sketch, "E1.2.0.155", {"position": v(69.72, 29.4) * mm});
            skPoint(sketch, "E1.2.0.156", {"position": v(69.72, 29.64) * mm});
            skLineSegment(sketch, "E1.2.0.161", {"start": v(69.13, 31.64) * mm, "end": v(67.89, 31.64) * mm});
            skLineSegment(sketch, "E1.2.0.162", {"start": v(69.13, 31.4) * mm, "end": v(67.89, 31.4) * mm});
            skLineSegment(sketch, "E1.2.0.163", {"start": v(67.89, 30.64) * mm, "end": v(68.32, 30.64) * mm});
            skLineSegment(sketch, "E1.2.0.166", {"start": v(67.89, 30.4) * mm, "end": v(68.32, 30.4) * mm});
            skLineSegment(sketch, "E1.2.0.171", {"start": v(69.13, 29.64) * mm, "end": v(67.89, 29.64) * mm});
            skLineSegment(sketch, "E1.2.0.173", {"start": v(69.13, 29.4) * mm, "end": v(67.89, 29.4) * mm});
            skLineSegment(sketch, "E1.2.0.174", {"start": v(69.13, 27.64) * mm, "end": v(67.89, 27.64) * mm});
            skArc(sketch, "E1.2.0.175", {"start": v(68.47, 28.22) * mm, "mid": v(68.53, 28.08) * mm, "end": v(68.67, 28.02) * mm});
            skLineSegment(sketch, "E1.2.0.176", {"start": v(67.89, 28.4) * mm, "end": v(68.32, 28.4) * mm});
            skLineSegment(sketch, "E1.2.0.177", {"start": v(67.89, 28.64) * mm, "end": v(68.32, 28.64) * mm});
            skLineSegment(sketch, "E1.2.0.180", {"start": v(70.52, 32.02) * mm, "end": v(69.92, 32.02) * mm});
            skLineSegment(sketch, "E1.2.0.185", {"start": v(71.17, 31.64) * mm, "end": v(70.87, 31.64) * mm});
            skLineSegment(sketch, "E1.2.0.194", {"start": v(69.13, 27.4) * mm, "end": v(67.89, 27.4) * mm});
            skLineSegment(sketch, "E1.2.0.205", {"start": v(71.17, 31.4) * mm, "end": v(70.87, 31.4) * mm});
            skArc(sketch, "E1.2.0.215", {"start": v(69.57, 31.64) * mm, "mid": v(69.68, 31.69) * mm, "end": v(69.72, 31.8) * mm});
            skArc(sketch, "E1.2.0.216", {"start": v(70.72, 31.82) * mm, "mid": v(70.66, 31.96) * mm, "end": v(70.52, 32.02) * mm});
            skArc(sketch, "E1.2.0.218", {"start": v(70.72, 31.8) * mm, "mid": v(70.77, 31.69) * mm, "end": v(70.87, 31.64) * mm});
            skLineSegment(sketch, "E1.2.0.222", {"start": v(71.17, 29.64) * mm, "end": v(70.87, 29.64) * mm});
            skLineSegment(sketch, "E1.2.0.228", {"start": v(69.72, 31.8) * mm, "end": v(69.72, 31.82) * mm});
            skLineSegment(sketch, "E1.2.0.229", {"start": v(70.72, 31.8) * mm, "end": v(70.72, 31.82) * mm});
            skLineSegment(sketch, "E1.2.0.230", {"start": v(69.62, 30.64) * mm, "end": v(71.17, 30.64) * mm});
            skArc(sketch, "E1.2.0.231", {"start": v(69.92, 32.02) * mm, "mid": v(69.78, 31.96) * mm, "end": v(69.72, 31.82) * mm});
            skLineSegment(sketch, "E1.2.0.239", {"start": v(69.27, 31.02) * mm, "end": v(68.67, 31.02) * mm});
            skLineSegment(sketch, "E1.2.0.240", {"start": v(71.17, 29.4) * mm, "end": v(70.87, 29.4) * mm});
            skLineSegment(sketch, "E1.2.0.242", {"start": v(69.57, 31.64) * mm, "end": v(69.13, 31.64) * mm});
            skArc(sketch, "E1.2.0.243", {"start": v(69.47, 30.82) * mm, "mid": v(69.41, 30.96) * mm, "end": v(69.27, 31.02) * mm});
            skArc(sketch, "E1.2.0.244", {"start": v(69.72, 31.24) * mm, "mid": v(69.68, 31.35) * mm, "end": v(69.57, 31.4) * mm});
            skArc(sketch, "E1.2.0.246", {"start": v(70.87, 31.4) * mm, "mid": v(70.77, 31.35) * mm, "end": v(70.72, 31.24) * mm});
            skLineSegment(sketch, "E1.2.0.249", {"start": v(69.57, 31.4) * mm, "end": v(69.13, 31.4) * mm});
            skLineSegment(sketch, "E1.2.0.250", {"start": v(70.52, 31.02) * mm, "end": v(69.92, 31.02) * mm});
            skArc(sketch, "E1.2.0.251", {"start": v(70.52, 31.02) * mm, "mid": v(70.66, 31.08) * mm, "end": v(70.72, 31.22) * mm});
            skLineSegment(sketch, "E1.2.0.253", {"start": v(69.62, 30.4) * mm, "end": v(71.17, 30.4) * mm});
            skLineSegment(sketch, "E1.2.0.257", {"start": v(69.72, 31.22) * mm, "end": v(69.72, 31.24) * mm});
            skLineSegment(sketch, "E1.2.0.259", {"start": v(70.72, 31.22) * mm, "end": v(70.72, 31.24) * mm});
            skArc(sketch, "E1.2.0.260", {"start": v(68.32, 30.64) * mm, "mid": v(68.43, 30.69) * mm, "end": v(68.47, 30.8) * mm});
            skArc(sketch, "E1.2.0.264", {"start": v(68.67, 31.02) * mm, "mid": v(68.53, 30.96) * mm, "end": v(68.47, 30.82) * mm});
            skLineSegment(sketch, "E1.2.0.265", {"start": v(69.62, 28.64) * mm, "end": v(71.17, 28.64) * mm});
            skArc(sketch, "E1.2.0.266", {"start": v(69.47, 30.8) * mm, "mid": v(69.52, 30.69) * mm, "end": v(69.62, 30.64) * mm});
            skLineSegment(sketch, "E1.2.0.269", {"start": v(69.47, 30.8) * mm, "end": v(69.47, 30.82) * mm});
            skLineSegment(sketch, "E1.2.0.274", {"start": v(71.17, 27.4) * mm, "end": v(70.87, 27.4) * mm});
            skArc(sketch, "E1.2.0.275", {"start": v(68.47, 30.24) * mm, "mid": v(68.43, 30.35) * mm, "end": v(68.32, 30.4) * mm});
            skLineSegment(sketch, "E1.2.0.276", {"start": v(71.17, 27.64) * mm, "end": v(70.87, 27.64) * mm});
            skArc(sketch, "E1.2.0.278", {"start": v(69.72, 31.22) * mm, "mid": v(69.78, 31.08) * mm, "end": v(69.92, 31.02) * mm});
            skArc(sketch, "E1.2.0.280", {"start": v(69.62, 30.4) * mm, "mid": v(69.52, 30.35) * mm, "end": v(69.47, 30.24) * mm});
            skLineSegment(sketch, "E1.2.0.284", {"start": v(69.62, 28.4) * mm, "end": v(71.17, 28.4) * mm});
            skLineSegment(sketch, "E1.2.0.285", {"start": v(68.47, 30.8) * mm, "end": v(68.47, 30.82) * mm});
            skLineSegment(sketch, "E1.2.0.288", {"start": v(70.52, 29.02) * mm, "end": v(69.92, 29.02) * mm});
            skArc(sketch, "E1.2.0.289", {"start": v(69.47, 28.82) * mm, "mid": v(69.41, 28.96) * mm, "end": v(69.27, 29.02) * mm});
            skLineSegment(sketch, "E1.2.0.290", {"start": v(70.52, 30.02) * mm, "end": v(69.92, 30.02) * mm});
            skLineSegment(sketch, "E1.2.0.292", {"start": v(69.27, 29.02) * mm, "end": v(68.67, 29.02) * mm});
            skLineSegment(sketch, "E1.2.0.293", {"start": v(69.27, 28.02) * mm, "end": v(68.67, 28.02) * mm});
            skLineSegment(sketch, "E1.2.0.295", {"start": v(69.57, 29.64) * mm, "end": v(69.13, 29.64) * mm});
            skArc(sketch, "E1.2.0.298", {"start": v(69.92, 30.02) * mm, "mid": v(69.78, 29.96) * mm, "end": v(69.72, 29.82) * mm});
            skArc(sketch, "E1.2.0.299", {"start": v(69.57, 29.64) * mm, "mid": v(69.68, 29.69) * mm, "end": v(69.72, 29.8) * mm});
            skArc(sketch, "E1.2.0.301", {"start": v(70.72, 29.82) * mm, "mid": v(70.66, 29.96) * mm, "end": v(70.52, 30.02) * mm});
            skArc(sketch, "E1.2.0.304", {"start": v(68.47, 28.24) * mm, "mid": v(68.43, 28.35) * mm, "end": v(68.32, 28.4) * mm});
            skArc(sketch, "E1.2.0.305", {"start": v(68.67, 29.02) * mm, "mid": v(68.53, 28.96) * mm, "end": v(68.47, 28.82) * mm});
            skArc(sketch, "E1.2.0.308", {"start": v(69.62, 28.4) * mm, "mid": v(69.52, 28.35) * mm, "end": v(69.47, 28.24) * mm});
            skLineSegment(sketch, "E1.2.0.311", {"start": v(69.27, 30.02) * mm, "end": v(68.67, 30.02) * mm});
            skLineSegment(sketch, "E1.2.0.312", {"start": v(69.72, 29.22) * mm, "end": v(69.72, 29.24) * mm});
            skLineSegment(sketch, "E1.2.0.315", {"start": v(70.72, 29.22) * mm, "end": v(70.72, 29.24) * mm});
            skArc(sketch, "E1.2.0.316", {"start": v(70.72, 29.8) * mm, "mid": v(70.77, 29.69) * mm, "end": v(70.87, 29.64) * mm});
            skArc(sketch, "E1.2.0.317", {"start": v(69.92, 28.02) * mm, "mid": v(69.78, 27.96) * mm, "end": v(69.72, 27.82) * mm});
            skLineSegment(sketch, "E1.2.0.326", {"start": v(68.47, 30.22) * mm, "end": v(68.47, 30.24) * mm});
            skLineSegment(sketch, "E1.2.0.327", {"start": v(68.47, 28.8) * mm, "end": v(68.47, 28.82) * mm});
            skArc(sketch, "E1.2.0.328", {"start": v(70.72, 27.82) * mm, "mid": v(70.66, 27.96) * mm, "end": v(70.52, 28.02) * mm});
            skArc(sketch, "E1.2.0.333", {"start": v(69.27, 28.02) * mm, "mid": v(69.41, 28.08) * mm, "end": v(69.47, 28.22) * mm});
            skArc(sketch, "E1.2.0.337", {"start": v(70.52, 29.02) * mm, "mid": v(70.66, 29.08) * mm, "end": v(70.72, 29.22) * mm});
            skLineSegment(sketch, "E1.2.0.340", {"start": v(69.72, 29.8) * mm, "end": v(69.72, 29.82) * mm});
            skLineSegment(sketch, "E1.2.0.343", {"start": v(69.57, 29.4) * mm, "end": v(69.13, 29.4) * mm});
            skLineSegment(sketch, "E1.2.0.345", {"start": v(68.47, 28.22) * mm, "end": v(68.47, 28.24) * mm});
            skLineSegment(sketch, "E1.2.0.349", {"start": v(69.47, 28.22) * mm, "end": v(69.47, 28.24) * mm});
            skArc(sketch, "E1.2.0.356", {"start": v(69.72, 29.22) * mm, "mid": v(69.78, 29.08) * mm, "end": v(69.92, 29.02) * mm});
            skLineSegment(sketch, "E1.2.0.357", {"start": v(70.72, 29.8) * mm, "end": v(70.72, 29.82) * mm});
            skArc(sketch, "E1.2.0.363", {"start": v(69.27, 30.02) * mm, "mid": v(69.41, 30.08) * mm, "end": v(69.47, 30.22) * mm});
            skLineSegment(sketch, "E1.2.0.369", {"start": v(70.52, 28.02) * mm, "end": v(69.92, 28.02) * mm});
            skArc(sketch, "E1.2.0.371", {"start": v(68.47, 30.22) * mm, "mid": v(68.53, 30.08) * mm, "end": v(68.67, 30.02) * mm});
            skArc(sketch, "E1.2.0.374", {"start": v(70.52, 27.02) * mm, "mid": v(70.66, 27.08) * mm, "end": v(70.72, 27.22) * mm});
            skLineSegment(sketch, "E1.2.0.375", {"start": v(70.52, 27.02) * mm, "end": v(69.92, 27.02) * mm});
            skLineSegment(sketch, "E1.2.0.377", {"start": v(69.57, 27.4) * mm, "end": v(69.13, 27.4) * mm});
            skLineSegment(sketch, "E1.2.0.382", {"start": v(69.57, 27.64) * mm, "end": v(69.13, 27.64) * mm});
            skArc(sketch, "E1.2.0.383", {"start": v(69.47, 28.8) * mm, "mid": v(69.52, 28.69) * mm, "end": v(69.62, 28.64) * mm});
            skLineSegment(sketch, "E1.2.0.385", {"start": v(70.72, 27.8) * mm, "end": v(70.72, 27.82) * mm});
            skArc(sketch, "E1.2.0.386", {"start": v(69.72, 27.22) * mm, "mid": v(69.78, 27.08) * mm, "end": v(69.92, 27.02) * mm});
            skArc(sketch, "E1.2.0.390", {"start": v(69.57, 27.64) * mm, "mid": v(69.68, 27.69) * mm, "end": v(69.72, 27.8) * mm});
            skArc(sketch, "E1.2.0.397", {"start": v(68.32, 28.64) * mm, "mid": v(68.43, 28.69) * mm, "end": v(68.47, 28.8) * mm});
            skArc(sketch, "E1.2.0.399", {"start": v(70.72, 27.8) * mm, "mid": v(70.77, 27.69) * mm, "end": v(70.87, 27.64) * mm});
            skLineSegment(sketch, "E1.2.0.402", {"start": v(69.47, 28.8) * mm, "end": v(69.47, 28.82) * mm});
            skArc(sketch, "E1.2.0.403", {"start": v(70.87, 29.4) * mm, "mid": v(70.77, 29.35) * mm, "end": v(70.72, 29.24) * mm});
            skArc(sketch, "E1.2.0.410", {"start": v(69.72, 29.24) * mm, "mid": v(69.68, 29.35) * mm, "end": v(69.57, 29.4) * mm});
            skArc(sketch, "E1.2.0.418", {"start": v(69.72, 27.24) * mm, "mid": v(69.68, 27.35) * mm, "end": v(69.57, 27.4) * mm});
            skArc(sketch, "E1.2.0.421", {"start": v(70.87, 27.4) * mm, "mid": v(70.77, 27.35) * mm, "end": v(70.72, 27.24) * mm});
            skLineSegment(sketch, "E1.2.0.423", {"start": v(69.72, 27.8) * mm, "end": v(69.72, 27.82) * mm});
            skLineSegment(sketch, "E1.2.0.426", {"start": v(69.47, 30.22) * mm, "end": v(69.47, 30.24) * mm});
            skLineSegment(sketch, "E1.2.0.430", {"start": v(69.72, 27.22) * mm, "end": v(69.72, 27.24) * mm});
            skLineSegment(sketch, "E1.2.0.432", {"start": v(70.72, 27.22) * mm, "end": v(70.72, 27.24) * mm});
            skPoint(sketch, "E2.4.3.0", {"position": v(79.72, 32.02) * mm});
            skPoint(sketch, "E2.5.3.0", {"position": v(80.72, 32.02) * mm});
            skPoint(sketch, "E2.8.3.0", {"position": v(80.72, 31.64) * mm});
            skPoint(sketch, "E2.10.3.0", {"position": v(78.47, 28.02) * mm});
            skPoint(sketch, "E2.13.3.0", {"position": v(80.22, 31.52) * mm});
            skPoint(sketch, "E2.16.3.0", {"position": v(79.47, 30.02) * mm});
            skPoint(sketch, "E2.17.3.0", {"position": v(78.47, 29.02) * mm});
            skPoint(sketch, "E2.19.3.0", {"position": v(79.72, 28.02) * mm});
            skPoint(sketch, "E2.22.3.0", {"position": v(78.47, 30.02) * mm});
            skPoint(sketch, "E2.23.3.0", {"position": v(80.72, 27.4) * mm});
            skPoint(sketch, "E2.24.3.0", {"position": v(78.47, 30.64) * mm});
            skPoint(sketch, "E2.34.3.0", {"position": v(80.72, 29.02) * mm});
            skPoint(sketch, "E2.35.3.0", {"position": v(78.47, 31.02) * mm});
            skPoint(sketch, "E2.36.3.0", {"position": v(80.72, 28.02) * mm});
            skPoint(sketch, "E2.37.3.0", {"position": v(79.72, 29.02) * mm});
            skPoint(sketch, "E2.40.3.0", {"position": v(79.72, 31.64) * mm});
            skPoint(sketch, "E2.41.3.0", {"position": v(80.72, 29.64) * mm});
            skPoint(sketch, "E2.45.3.0", {"position": v(80.22, 31.52) * mm});
            skPoint(sketch, "E2.46.3.0", {"position": v(80.72, 31.4) * mm});
            skPoint(sketch, "E2.51.3.0", {"position": v(78.47, 28.4) * mm});
            skPoint(sketch, "E2.54.3.0", {"position": v(78.97, 30.52) * mm});
            skPoint(sketch, "E2.59.3.0", {"position": v(78.47, 28.64) * mm});
            skPoint(sketch, "E2.69.3.0", {"position": v(79.72, 27.64) * mm});
            skPoint(sketch, "E2.70.3.0", {"position": v(78.47, 30.4) * mm});
            skPoint(sketch, "E2.71.3.0", {"position": v(79.47, 28.4) * mm});
            skPoint(sketch, "E2.73.3.0", {"position": v(80.22, 27.52) * mm});
            skPoint(sketch, "E2.74.3.0", {"position": v(79.47, 28.64) * mm});
            skPoint(sketch, "E2.80.3.0", {"position": v(79.72, 31.4) * mm});
            skPoint(sketch, "E2.82.3.0", {"position": v(80.72, 30.02) * mm});
            skPoint(sketch, "E2.84.3.0", {"position": v(80.22, 27.52) * mm});
            skPoint(sketch, "E2.85.3.0", {"position": v(80.72, 29.4) * mm});
            skPoint(sketch, "E2.87.3.0", {"position": v(80.72, 31.02) * mm});
            skPoint(sketch, "E2.90.3.0", {"position": v(78.97, 28.52) * mm});
            skPoint(sketch, "E2.92.3.0", {"position": v(78.97, 30.52) * mm});
            skPoint(sketch, "E2.94.3.0", {"position": v(80.22, 29.52) * mm});
            skPoint(sketch, "E2.96.3.0", {"position": v(80.72, 27.64) * mm});
            skPoint(sketch, "E2.108.3.0", {"position": v(79.72, 27.4) * mm});
            skPoint(sketch, "E2.112.3.0", {"position": v(79.47, 29.02) * mm});
            skPoint(sketch, "E2.115.3.0", {"position": v(80.22, 29.52) * mm});
            skPoint(sketch, "E2.119.3.0", {"position": v(79.72, 31.02) * mm});
            skPoint(sketch, "E2.128.3.0", {"position": v(79.47, 28.02) * mm});
            skPoint(sketch, "E2.136.3.0", {"position": v(78.97, 28.52) * mm});
            skPoint(sketch, "E2.143.3.0", {"position": v(79.47, 30.64) * mm});
            skPoint(sketch, "E2.149.3.0", {"position": v(79.72, 30.02) * mm});
            skPoint(sketch, "E2.150.3.0", {"position": v(79.47, 31.02) * mm});
            skPoint(sketch, "E2.156.3.0", {"position": v(79.47, 30.4) * mm});
            skPoint(sketch, "E2.157.3.0", {"position": v(79.72, 29.4) * mm});
            skPoint(sketch, "E2.158.3.0", {"position": v(79.72, 29.64) * mm});
            skLineSegment(sketch, "E2.163.3.0", {"start": v(79.13, 31.64) * mm, "end": v(77.89, 31.64) * mm});
            skLineSegment(sketch, "E2.166.3.0", {"start": v(79.13, 31.4) * mm, "end": v(77.89, 31.4) * mm});
            skLineSegment(sketch, "E2.169.3.0", {"start": v(77.89, 30.64) * mm, "end": v(78.32, 30.64) * mm});
            skLineSegment(sketch, "E2.178.3.0", {"start": v(77.89, 30.4) * mm, "end": v(78.32, 30.4) * mm});
            skLineSegment(sketch, "E2.193.3.0", {"start": v(79.13, 29.64) * mm, "end": v(77.89, 29.64) * mm});
            skLineSegment(sketch, "E2.199.3.0", {"start": v(79.13, 29.4) * mm, "end": v(77.89, 29.4) * mm});
            skLineSegment(sketch, "E2.202.3.0", {"start": v(79.13, 27.64) * mm, "end": v(77.89, 27.64) * mm});
            skArc(sketch, "E2.205.3.0", {"start": v(78.47, 28.22) * mm, "mid": v(78.53, 28.08) * mm, "end": v(78.67, 28.02) * mm});
            skLineSegment(sketch, "E2.209.3.0", {"start": v(77.89, 28.4) * mm, "end": v(78.32, 28.4) * mm});
            skLineSegment(sketch, "E2.212.3.0", {"start": v(77.89, 28.64) * mm, "end": v(78.32, 28.64) * mm});
            skLineSegment(sketch, "E2.221.3.0", {"start": v(80.52, 32.02) * mm, "end": v(79.92, 32.02) * mm});
            skLineSegment(sketch, "E2.263.3.0", {"start": v(79.13, 27.4) * mm, "end": v(77.89, 27.4) * mm});
            skArc(sketch, "E2.328.3.0", {"start": v(79.57, 31.64) * mm, "mid": v(79.68, 31.69) * mm, "end": v(79.72, 31.8) * mm});
            skArc(sketch, "E2.332.3.0", {"start": v(80.72, 31.82) * mm, "mid": v(80.66, 31.96) * mm, "end": v(80.52, 32.02) * mm});
            skLineSegment(sketch, "E2.370.3.0", {"start": v(79.72, 31.8) * mm, "end": v(79.72, 31.82) * mm});
            skLineSegment(sketch, "E2.373.3.0", {"start": v(80.72, 31.8) * mm, "end": v(80.72, 31.82) * mm});
            skArc(sketch, "E2.379.3.0", {"start": v(79.92, 32.02) * mm, "mid": v(79.78, 31.96) * mm, "end": v(79.72, 31.82) * mm});
            skLineSegment(sketch, "E2.404.3.0", {"start": v(79.27, 31.02) * mm, "end": v(78.67, 31.02) * mm});
            skLineSegment(sketch, "E2.413.3.0", {"start": v(79.57, 31.64) * mm, "end": v(79.13, 31.64) * mm});
            skArc(sketch, "E2.416.3.0", {"start": v(79.47, 30.82) * mm, "mid": v(79.41, 30.96) * mm, "end": v(79.27, 31.02) * mm});
            skArc(sketch, "E2.420.3.0", {"start": v(79.72, 31.24) * mm, "mid": v(79.68, 31.35) * mm, "end": v(79.57, 31.4) * mm});
            skLineSegment(sketch, "E2.437.3.0", {"start": v(79.57, 31.4) * mm, "end": v(79.13, 31.4) * mm});
            skLineSegment(sketch, "E2.440.3.0", {"start": v(80.52, 31.02) * mm, "end": v(79.92, 31.02) * mm});
            skArc(sketch, "E2.443.3.0", {"start": v(80.52, 31.02) * mm, "mid": v(80.66, 31.08) * mm, "end": v(80.72, 31.22) * mm});
            skLineSegment(sketch, "E2.463.3.0", {"start": v(79.72, 31.22) * mm, "end": v(79.72, 31.24) * mm});
            skLineSegment(sketch, "E2.469.3.0", {"start": v(80.72, 31.22) * mm, "end": v(80.72, 31.24) * mm});
            skArc(sketch, "E2.472.3.0", {"start": v(78.32, 30.64) * mm, "mid": v(78.43, 30.69) * mm, "end": v(78.47, 30.8) * mm});
            skArc(sketch, "E2.485.3.0", {"start": v(78.67, 31.02) * mm, "mid": v(78.53, 30.96) * mm, "end": v(78.47, 30.82) * mm});
            skLineSegment(sketch, "E2.502.3.0", {"start": v(79.47, 30.8) * mm, "end": v(79.47, 30.82) * mm});
            skArc(sketch, "E2.520.3.0", {"start": v(78.47, 30.24) * mm, "mid": v(78.43, 30.35) * mm, "end": v(78.32, 30.4) * mm});
            skArc(sketch, "E2.530.3.0", {"start": v(79.72, 31.22) * mm, "mid": v(79.78, 31.08) * mm, "end": v(79.92, 31.02) * mm});
            skLineSegment(sketch, "E2.554.3.0", {"start": v(78.47, 30.8) * mm, "end": v(78.47, 30.82) * mm});
            skLineSegment(sketch, "E2.564.3.0", {"start": v(80.52, 29.02) * mm, "end": v(79.92, 29.02) * mm});
            skArc(sketch, "E2.567.3.0", {"start": v(79.47, 28.82) * mm, "mid": v(79.41, 28.96) * mm, "end": v(79.27, 29.02) * mm});
            skLineSegment(sketch, "E2.571.3.0", {"start": v(80.52, 30.02) * mm, "end": v(79.92, 30.02) * mm});
            skLineSegment(sketch, "E2.577.3.0", {"start": v(79.27, 29.02) * mm, "end": v(78.67, 29.02) * mm});
            skLineSegment(sketch, "E2.580.3.0", {"start": v(79.27, 28.02) * mm, "end": v(78.67, 28.02) * mm});
            skLineSegment(sketch, "E2.586.3.0", {"start": v(79.57, 29.64) * mm, "end": v(79.13, 29.64) * mm});
            skArc(sketch, "E2.596.3.0", {"start": v(79.92, 30.02) * mm, "mid": v(79.78, 29.96) * mm, "end": v(79.72, 29.82) * mm});
            skArc(sketch, "E2.600.3.0", {"start": v(79.57, 29.64) * mm, "mid": v(79.68, 29.69) * mm, "end": v(79.72, 29.8) * mm});
            skArc(sketch, "E2.607.3.0", {"start": v(80.72, 29.82) * mm, "mid": v(80.66, 29.96) * mm, "end": v(80.52, 30.02) * mm});
            skArc(sketch, "E2.618.3.0", {"start": v(78.47, 28.24) * mm, "mid": v(78.43, 28.35) * mm, "end": v(78.32, 28.4) * mm});
            skArc(sketch, "E2.622.3.0", {"start": v(78.67, 29.02) * mm, "mid": v(78.53, 28.96) * mm, "end": v(78.47, 28.82) * mm});
            skLineSegment(sketch, "E2.645.3.0", {"start": v(79.27, 30.02) * mm, "end": v(78.67, 30.02) * mm});
            skLineSegment(sketch, "E2.648.3.0", {"start": v(79.72, 29.22) * mm, "end": v(79.72, 29.24) * mm});
            skLineSegment(sketch, "E2.658.3.0", {"start": v(80.72, 29.22) * mm, "end": v(80.72, 29.24) * mm});
            skArc(sketch, "E2.665.3.0", {"start": v(79.92, 28.02) * mm, "mid": v(79.78, 27.96) * mm, "end": v(79.72, 27.82) * mm});
            skLineSegment(sketch, "E2.693.3.0", {"start": v(78.47, 30.22) * mm, "end": v(78.47, 30.24) * mm});
            skLineSegment(sketch, "E2.696.3.0", {"start": v(78.47, 28.8) * mm, "end": v(78.47, 28.82) * mm});
            skArc(sketch, "E2.699.3.0", {"start": v(80.72, 27.82) * mm, "mid": v(80.66, 27.96) * mm, "end": v(80.52, 28.02) * mm});
            skArc(sketch, "E2.715.3.0", {"start": v(79.27, 28.02) * mm, "mid": v(79.41, 28.08) * mm, "end": v(79.47, 28.22) * mm});
            skArc(sketch, "E2.730.3.0", {"start": v(80.52, 29.02) * mm, "mid": v(80.66, 29.08) * mm, "end": v(80.72, 29.22) * mm});
            skLineSegment(sketch, "E2.742.3.0", {"start": v(79.72, 29.8) * mm, "end": v(79.72, 29.82) * mm});
            skLineSegment(sketch, "E2.751.3.0", {"start": v(79.57, 29.4) * mm, "end": v(79.13, 29.4) * mm});
            skLineSegment(sketch, "E2.758.3.0", {"start": v(78.47, 28.22) * mm, "end": v(78.47, 28.24) * mm});
            skLineSegment(sketch, "E2.773.3.0", {"start": v(79.47, 28.22) * mm, "end": v(79.47, 28.24) * mm});
            skArc(sketch, "E2.799.3.0", {"start": v(79.72, 29.22) * mm, "mid": v(79.78, 29.08) * mm, "end": v(79.92, 29.02) * mm});
            skLineSegment(sketch, "E2.803.3.0", {"start": v(80.72, 29.8) * mm, "end": v(80.72, 29.82) * mm});
            skArc(sketch, "E2.825.3.0", {"start": v(79.27, 30.02) * mm, "mid": v(79.41, 30.08) * mm, "end": v(79.47, 30.22) * mm});
            skLineSegment(sketch, "E2.848.3.0", {"start": v(80.52, 28.02) * mm, "end": v(79.92, 28.02) * mm});
            skArc(sketch, "E2.855.3.0", {"start": v(78.47, 30.22) * mm, "mid": v(78.53, 30.08) * mm, "end": v(78.67, 30.02) * mm});
            skArc(sketch, "E2.866.3.0", {"start": v(80.52, 27.02) * mm, "mid": v(80.66, 27.08) * mm, "end": v(80.72, 27.22) * mm});
            skLineSegment(sketch, "E2.870.3.0", {"start": v(80.52, 27.02) * mm, "end": v(79.92, 27.02) * mm});
            skLineSegment(sketch, "E2.877.3.0", {"start": v(79.57, 27.4) * mm, "end": v(79.13, 27.4) * mm});
            skLineSegment(sketch, "E2.894.3.0", {"start": v(79.57, 27.64) * mm, "end": v(79.13, 27.64) * mm});
            skLineSegment(sketch, "E2.904.3.0", {"start": v(80.72, 27.8) * mm, "end": v(80.72, 27.82) * mm});
            skArc(sketch, "E2.907.3.0", {"start": v(79.72, 27.22) * mm, "mid": v(79.78, 27.08) * mm, "end": v(79.92, 27.02) * mm});
            skArc(sketch, "E2.922.3.0", {"start": v(79.57, 27.64) * mm, "mid": v(79.68, 27.69) * mm, "end": v(79.72, 27.8) * mm});
            skArc(sketch, "E2.947.3.0", {"start": v(78.32, 28.64) * mm, "mid": v(78.43, 28.69) * mm, "end": v(78.47, 28.8) * mm});
            skLineSegment(sketch, "E2.965.3.0", {"start": v(79.47, 28.8) * mm, "end": v(79.47, 28.82) * mm});
            skArc(sketch, "E2.992.3.0", {"start": v(79.72, 29.24) * mm, "mid": v(79.68, 29.35) * mm, "end": v(79.57, 29.4) * mm});
            skArc(sketch, "E2.1020.3.0", {"start": v(79.72, 27.24) * mm, "mid": v(79.68, 27.35) * mm, "end": v(79.57, 27.4) * mm});
            skLineSegment(sketch, "E2.1038.3.0", {"start": v(79.72, 27.8) * mm, "end": v(79.72, 27.82) * mm});
            skLineSegment(sketch, "E2.1049.3.0", {"start": v(79.47, 30.22) * mm, "end": v(79.47, 30.24) * mm});
            skLineSegment(sketch, "E2.1063.3.0", {"start": v(79.72, 27.22) * mm, "end": v(79.72, 27.24) * mm});
            skLineSegment(sketch, "E2.1070.3.0", {"start": v(80.72, 27.22) * mm, "end": v(80.72, 27.24) * mm});
            skLineSegment(sketch, "E3", {"start": v(71.17, 31.64) * mm, "end": v(77.89, 31.64) * mm});
            skLineSegment(sketch, "E4", {"start": v(71.17, 31.4) * mm, "end": v(77.89, 31.4) * mm});
            skLineSegment(sketch, "E5", {"start": v(71.17, 30.64) * mm, "end": v(77.89, 30.64) * mm});
            skLineSegment(sketch, "E6", {"start": v(71.17, 30.4) * mm, "end": v(77.89, 30.4) * mm});
            skLineSegment(sketch, "E7", {"start": v(80.72, 31.8) * mm, "end": v(80.72, 31.64) * mm});
            skLineSegment(sketch, "E8", {"start": v(79.47, 30.8) * mm, "end": v(79.47, 30.64) * mm});
            skLineSegment(sketch, "E9", {"start": v(80.72, 29.8) * mm, "end": v(80.72, 29.64) * mm});
            skLineSegment(sketch, "E10", {"start": v(79.47, 28.8) * mm, "end": v(79.47, 28.64) * mm});
            skLineSegment(sketch, "E11", {"start": v(80.72, 27.8) * mm, "end": v(80.72, 27.64) * mm});
            skLineSegment(sketch, "E12", {"start": v(71.17, 29.64) * mm, "end": v(77.89, 29.64) * mm});
            skLineSegment(sketch, "E13", {"start": v(77.89, 29.4) * mm, "end": v(71.17, 29.4) * mm});
            skLineSegment(sketch, "E14", {"start": v(71.17, 28.64) * mm, "end": v(77.89, 28.64) * mm});
            skLineSegment(sketch, "E15", {"start": v(77.89, 28.4) * mm, "end": v(71.17, 28.4) * mm});
            skLineSegment(sketch, "E16", {"start": v(71.17, 27.64) * mm, "end": v(77.89, 27.64) * mm});
            skLineSegment(sketch, "E17", {"start": v(77.89, 27.4) * mm, "end": v(71.17, 27.4) * mm});
            skLineSegment(sketch, "E18", {"start": v(67.89, 31.64) * mm, "end": v(61.17, 31.64) * mm});
            skLineSegment(sketch, "E19", {"start": v(67.89, 31.4) * mm, "end": v(61.17, 31.4) * mm});
            skLineSegment(sketch, "E20", {"start": v(67.89, 30.64) * mm, "end": v(61.17, 30.64) * mm});
            skLineSegment(sketch, "E21", {"start": v(67.89, 30.4) * mm, "end": v(61.17, 30.4) * mm});
            skLineSegment(sketch, "E22", {"start": v(67.89, 29.64) * mm, "end": v(61.17, 29.64) * mm});
            skLineSegment(sketch, "E23", {"start": v(67.89, 29.4) * mm, "end": v(61.17, 29.4) * mm});
            skLineSegment(sketch, "E24", {"start": v(67.89, 28.64) * mm, "end": v(61.17, 28.64) * mm});
            skLineSegment(sketch, "E25", {"start": v(67.89, 28.4) * mm, "end": v(61.17, 28.4) * mm});
            skLineSegment(sketch, "E26", {"start": v(67.89, 27.64) * mm, "end": v(61.17, 27.64) * mm});
            skLineSegment(sketch, "E27", {"start": v(67.89, 27.4) * mm, "end": v(61.17, 27.4) * mm});
            skLineSegment(sketch, "E28", {"start": v(51.17, 31.64) * mm, "end": v(57.89, 31.64) * mm});
            skLineSegment(sketch, "E29", {"start": v(57.89, 31.4) * mm, "end": v(51.17, 31.4) * mm});
            skLineSegment(sketch, "E30", {"start": v(51.17, 30.64) * mm, "end": v(57.89, 30.64) * mm});
            skLineSegment(sketch, "E31", {"start": v(57.89, 30.4) * mm, "end": v(51.17, 30.4) * mm});
            skLineSegment(sketch, "E32", {"start": v(51.17, 29.64) * mm, "end": v(57.89, 29.64) * mm});
            skLineSegment(sketch, "E33", {"start": v(57.89, 29.4) * mm, "end": v(51.17, 29.4) * mm});
            skLineSegment(sketch, "E34", {"start": v(57.89, 28.64) * mm, "end": v(51.17, 28.64) * mm});
            skLineSegment(sketch, "E35", {"start": v(57.89, 28.4) * mm, "end": v(51.17, 28.4) * mm});
            skLineSegment(sketch, "E36", {"start": v(57.89, 27.64) * mm, "end": v(51.17, 27.64) * mm});
            skLineSegment(sketch, "E37", {"start": v(57.89, 27.4) * mm, "end": v(51.17, 27.4) * mm});
            skLineSegment(sketch, "E38", {"start": v(47.89, 30.64) * mm, "end": v(46.76, 30.64) * mm});
            skLineSegment(sketch, "E39", {"start": v(47.89, 30.4) * mm, "end": v(46.76, 30.4) * mm});
            skLineSegment(sketch, "E40", {"start": v(47.89, 28.64) * mm, "end": v(46.76, 28.64) * mm});
            skLineSegment(sketch, "E41", {"start": v(47.89, 28.4) * mm, "end": v(46.76, 28.4) * mm});
            skLineSegment(sketch, "E42", {"start": v(47.89, 31.64) * mm, "end": v(43.7, 31.64) * mm});
            skLineSegment(sketch, "E43", {"start": v(47.89, 27.4) * mm, "end": v(43.7, 27.4) * mm});
            skLineSegment(sketch, "E44", {"start": v(46.64, 30.77) * mm, "end": v(46.64, 31.26) * mm});
            skLineSegment(sketch, "E45", {"start": v(46.64, 30.26) * mm, "end": v(46.64, 29.77) * mm});
            skLineSegment(sketch, "E46", {"start": v(46.64, 28.26) * mm, "end": v(46.64, 27.77) * mm});
            skLineSegment(sketch, "E47", {"start": v(47.89, 27.64) * mm, "end": v(46.76, 27.64) * mm});
            skLineSegment(sketch, "E48", {"start": v(47.89, 29.4) * mm, "end": v(46.76, 29.4) * mm});
            skLineSegment(sketch, "E49", {"start": v(46.76, 29.64) * mm, "end": v(47.89, 29.64) * mm});
            skLineSegment(sketch, "E50", {"start": v(47.89, 31.4) * mm, "end": v(46.76, 31.4) * mm});
            skLineSegment(sketch, "E51", {"start": v(42.62, 28.46) * mm, "end": v(42.62, 30.58) * mm});
            skPoint(sketch, "E52.visualSharp", {"position": v(42.62, 31.64) * mm});
            skArc(sketch, "E52.filletArc", {"start": v(43.7, 31.64) * mm, "mid": v(42.94, 31.33) * mm, "end": v(42.62, 30.58) * mm});
            skPoint(sketch, "E53.visualSharp", {"position": v(42.62, 27.4) * mm});
            skArc(sketch, "E53.filletArc", {"start": v(42.62, 28.46) * mm, "mid": v(42.94, 27.7) * mm, "end": v(43.7, 27.4) * mm});
            skPoint(sketch, "E54.visualSharp", {"position": v(46.64, 31.4) * mm});
            skArc(sketch, "E54.filletArc", {"start": v(46.76, 31.4) * mm, "mid": v(46.67, 31.35) * mm, "end": v(46.64, 31.26) * mm});
            skPoint(sketch, "E55.visualSharp", {"position": v(46.64, 30.64) * mm});
            skArc(sketch, "E55.filletArc", {"start": v(46.64, 30.77) * mm, "mid": v(46.67, 30.68) * mm, "end": v(46.76, 30.64) * mm});
            skPoint(sketch, "E56.visualSharp", {"position": v(46.64, 30.4) * mm});
            skArc(sketch, "E56.filletArc", {"start": v(46.76, 30.4) * mm, "mid": v(46.67, 30.35) * mm, "end": v(46.64, 30.26) * mm});
            skPoint(sketch, "E57.visualSharp", {"position": v(46.64, 28.64) * mm});
            skArc(sketch, "E57.filletArc", {"start": v(46.64, 28.77) * mm, "mid": v(46.67, 28.68) * mm, "end": v(46.76, 28.64) * mm});
            skPoint(sketch, "E58.visualSharp", {"position": v(46.64, 28.4) * mm});
            skArc(sketch, "E58.filletArc", {"start": v(46.76, 28.4) * mm, "mid": v(46.67, 28.35) * mm, "end": v(46.64, 28.26) * mm});
            skPoint(sketch, "E59.visualSharp", {"position": v(46.64, 27.64) * mm});
            skArc(sketch, "E59.filletArc", {"start": v(46.64, 27.77) * mm, "mid": v(46.67, 27.68) * mm, "end": v(46.76, 27.64) * mm});
            skLineSegment(sketch, "E60.trimOffspring", {"start": v(46.64, 29.26) * mm, "end": v(46.64, 28.77) * mm});
            skPoint(sketch, "E61.visualSharp", {"position": v(46.64, 29.64) * mm});
            skArc(sketch, "E61.filletArc", {"start": v(46.64, 29.77) * mm, "mid": v(46.67, 29.68) * mm, "end": v(46.76, 29.64) * mm});
            skPoint(sketch, "E62.visualSharp", {"position": v(46.64, 29.4) * mm});
            skArc(sketch, "E62.filletArc", {"start": v(46.76, 29.4) * mm, "mid": v(46.67, 29.35) * mm, "end": v(46.64, 29.26) * mm});
            skLineSegment(sketch, "E63", {"start": v(80.88, 28.38) * mm, "end": v(82, 28.38) * mm});
            skLineSegment(sketch, "E64", {"start": v(80.88, 28.63) * mm, "end": v(82, 28.63) * mm});
            skLineSegment(sketch, "E65", {"start": v(80.88, 30.38) * mm, "end": v(82, 30.38) * mm});
            skLineSegment(sketch, "E66", {"start": v(80.88, 30.63) * mm, "end": v(82, 30.63) * mm});
            skLineSegment(sketch, "E67", {"start": v(80.88, 27.38) * mm, "end": v(82.13, 27.38) * mm});
            skLineSegment(sketch, "E68", {"start": v(80.88, 31.63) * mm, "end": v(82.13, 31.63) * mm});
            skLineSegment(sketch, "E69", {"start": v(80.88, 31.38) * mm, "end": v(82, 31.38) * mm});
            skLineSegment(sketch, "E70", {"start": v(80.88, 29.63) * mm, "end": v(82, 29.63) * mm});
            skLineSegment(sketch, "E71", {"start": v(82, 29.38) * mm, "end": v(80.88, 29.38) * mm});
            skLineSegment(sketch, "E72", {"start": v(80.88, 27.63) * mm, "end": v(82, 27.63) * mm});
            skPoint(sketch, "E73.visualSharp", {"position": v(86.14, 27.38) * mm});
            skPoint(sketch, "E74.visualSharp", {"position": v(86.14, 31.63) * mm});
            skPoint(sketch, "E75.visualSharp", {"position": v(82.13, 27.63) * mm});
            skArc(sketch, "E75.filletArc", {"start": v(82, 27.63) * mm, "mid": v(82.1, 27.67) * mm, "end": v(82.13, 27.76) * mm});
            skPoint(sketch, "E76.visualSharp", {"position": v(82.13, 28.38) * mm});
            skArc(sketch, "E76.filletArc", {"start": v(82.13, 28.25) * mm, "mid": v(82.1, 28.34) * mm, "end": v(82, 28.38) * mm});
            skPoint(sketch, "E77.visualSharp", {"position": v(82.13, 28.63) * mm});
            skArc(sketch, "E77.filletArc", {"start": v(82, 28.63) * mm, "mid": v(82.1, 28.67) * mm, "end": v(82.13, 28.76) * mm});
            skPoint(sketch, "E78.visualSharp", {"position": v(82.13, 30.38) * mm});
            skArc(sketch, "E78.filletArc", {"start": v(82.13, 30.25) * mm, "mid": v(82.1, 30.34) * mm, "end": v(82, 30.38) * mm});
            skPoint(sketch, "E79.visualSharp", {"position": v(82.13, 30.63) * mm});
            skArc(sketch, "E79.filletArc", {"start": v(82, 30.63) * mm, "mid": v(82.1, 30.67) * mm, "end": v(82.13, 30.76) * mm});
            skPoint(sketch, "E80.visualSharp", {"position": v(82.13, 31.38) * mm});
            skArc(sketch, "E80.filletArc", {"start": v(82.13, 31.25) * mm, "mid": v(82.1, 31.34) * mm, "end": v(82, 31.38) * mm});
            skPoint(sketch, "E81.visualSharp", {"position": v(82.13, 29.38) * mm});
            skArc(sketch, "E81.filletArc", {"start": v(82.13, 29.25) * mm, "mid": v(82.1, 29.34) * mm, "end": v(82, 29.38) * mm});
            skPoint(sketch, "E82.visualSharp", {"position": v(82.13, 29.63) * mm});
            skArc(sketch, "E82.filletArc", {"start": v(82, 29.63) * mm, "mid": v(82.1, 29.67) * mm, "end": v(82.13, 29.76) * mm});
            skLineSegment(sketch, "E83.trimOffspring", {"start": v(80.72, 31.4) * mm, "end": v(80.72, 31.24) * mm});
            skLineSegment(sketch, "E84.trimOffspring", {"start": v(79.47, 30.4) * mm, "end": v(79.47, 30.24) * mm});
            skLineSegment(sketch, "E85.trimOffspring", {"start": v(80.72, 29.4) * mm, "end": v(80.72, 29.24) * mm});
            skLineSegment(sketch, "E86.trimOffspring", {"start": v(79.47, 28.4) * mm, "end": v(79.47, 28.24) * mm});
            skLineSegment(sketch, "E87.trimOffspring", {"start": v(80.72, 27.4) * mm, "end": v(80.72, 27.24) * mm});
            skLineSegment(sketch, "E88", {"start": v(80.72, 31.64) * mm, "end": v(80.88, 31.63) * mm});
            skLineSegment(sketch, "E89", {"start": v(80.72, 31.4) * mm, "end": v(80.88, 31.38) * mm});
            skLineSegment(sketch, "E90", {"start": v(79.47, 30.64) * mm, "end": v(80.88, 30.63) * mm});
            skLineSegment(sketch, "E91", {"start": v(79.47, 30.4) * mm, "end": v(80.88, 30.38) * mm});
            skLineSegment(sketch, "E92", {"start": v(80.72, 29.64) * mm, "end": v(80.88, 29.63) * mm});
            skLineSegment(sketch, "E93", {"start": v(80.72, 29.4) * mm, "end": v(80.88, 29.38) * mm});
            skLineSegment(sketch, "E94", {"start": v(79.47, 28.64) * mm, "end": v(80.88, 28.63) * mm});
            skLineSegment(sketch, "E95", {"start": v(79.47, 28.4) * mm, "end": v(80.88, 28.38) * mm});
            skLineSegment(sketch, "E96", {"start": v(80.72, 27.64) * mm, "end": v(80.88, 27.63) * mm});
            skLineSegment(sketch, "E97", {"start": v(80.72, 27.4) * mm, "end": v(80.88, 27.38) * mm});
            skLineSegment(sketch, "E98", {"start": v(86.14, 30.56) * mm, "end": v(86.14, 28.44) * mm});
            skLineSegment(sketch, "E99", {"start": v(82.13, 31.25) * mm, "end": v(82.13, 30.76) * mm});
            skLineSegment(sketch, "E100", {"start": v(82.13, 30.25) * mm, "end": v(82.13, 29.76) * mm});
            skLineSegment(sketch, "E101", {"start": v(82.13, 29.25) * mm, "end": v(82.13, 28.76) * mm});
            skLineSegment(sketch, "E102", {"start": v(82.13, 28.25) * mm, "end": v(82.13, 27.76) * mm});
            skLineSegment(sketch, "E103.top", {"start": v(82.13, 33.63) * mm, "end": v(86.14, 33.63) * mm});
            skLineSegment(sketch, "E103.left", {"start": v(82.13, 31.63) * mm, "end": v(82.13, 33.63) * mm});
            skLineSegment(sketch, "E103.right", {"start": v(86.14, 31.63) * mm, "end": v(86.14, 33.63) * mm});
            skLineSegment(sketch, "E104.top", {"start": v(82.13, 25.4) * mm, "end": v(86.14, 25.4) * mm});
            skLineSegment(sketch, "E104.left", {"start": v(82.13, 27.38) * mm, "end": v(82.13, 25.4) * mm});
            skLineSegment(sketch, "E104.right", {"start": v(86.14, 27.38) * mm, "end": v(86.14, 25.4) * mm});
            skLineSegment(sketch, "E105", {"start": v(86.14, 31.63) * mm, "end": v(86.14, 27.38) * mm});
            skSolve(sketch);
        }
        {
            var Q0;
            Q0=makeQuery(id+"F0.imprint","IMPRINT",FACE,{"disambiguationData":[TD([[makeQuery(id+"F0.imprint","IMPRINT",EDGE,{"derivedFrom":sQuery(id+"F0.wireOp",EDGE,"E0.0.5.4")}),1.0]])]});
            extrude(context, id + "F1", {"entities" : qUnion([Q0]), "depth" : .25 * mm, "offsetDistance" : 25 * mm});
        }
        {
            var Q0;
            Q0=makeQuery(id+"F1.opExtrude","CAP_FACE",FACE,{"disambiguationData":[OSD([sQuery(id+"F0.wireOp",EDGE,"E0.0.5.4"),sQuery(id+"F0.wireOp",EDGE,"E0.0.5.5"),sQuery(id+"F0.wireOp",EDGE,"E0.0.5.6"),sQuery(id+"F0.wireOp",EDGE,"E0.0.5.7"),sQuery(id+"F0.wireOp",EDGE,"E0.0.5.18"),sQuery(id+"F0.wireOp",EDGE,"E0.0.5.19"),sQuery(id+"F0.wireOp",EDGE,"E0.0.5.32"),sQuery(id+"F0.wireOp",EDGE,"E0.0.5.33"),sQuery(id+"F0.wireOp",EDGE,"E0.0.5.34"),sQuery(id+"F0.wireOp",EDGE,"E0.0.5.41"),sQuery(id+"F0.wireOp",EDGE,"E0.0.5.44"),sQuery(id+"F0.wireOp",EDGE,"E0.0.5.45"),sQuery(id+"F0.wireOp",EDGE,"E0.0.5.46"),sQuery(id+"F0.wireOp",EDGE,"E0.0.5.49"),sQuery(id+"F0.wireOp",EDGE,"E0.0.5.50"),sQuery(id+"F0.wireOp",EDGE,"E0.0.5.55"),sQuery(id+"F0.wireOp",EDGE,"E0.0.5.56"),sQuery(id+"F0.wireOp",EDGE,"E0.0.5.57"),sQuery(id+"F0.wireOp",EDGE,"E0.0.5.60"),sQuery(id+"F0.wireOp",EDGE,"E0.0.5.61"),sQuery(id+"F0.wireOp",EDGE,"E0.0.6.0"),sQuery(id+"F0.wireOp",EDGE,"E0.0.6.1"),sQuery(id+"F0.wireOp",EDGE,"E0.0.6.2"),sQuery(id+"F0.wireOp",EDGE,"E0.0.6.3"),sQuery(id+"F0.wireOp",EDGE,"E0.0.6.4"),sQuery(id+"F0.wireOp",EDGE,"E0.0.6.5"),sQuery(id+"F0.wireOp",EDGE,"E0.0.6.6"),sQuery(id+"F0.wireOp",EDGE,"E0.0.6.7"),sQuery(id+"F0.wireOp",EDGE,"E0.0.6.18"),sQuery(id+"F0.wireOp",EDGE,"E0.0.6.19"),sQuery(id+"F0.wireOp",EDGE,"E0.0.6.22"),sQuery(id+"F0.wireOp",EDGE,"E0.0.6.25"),sQuery(id+"F0.wireOp",EDGE,"E0.0.6.32"),sQuery(id+"F0.wireOp",EDGE,"E0.0.6.33"),sQuery(id+"F0.wireOp",EDGE,"E0.0.6.34"),sQuery(id+"F0.wireOp",EDGE,"E0.0.6.35"),sQuery(id+"F0.wireOp",EDGE,"E0.0.6.36"),sQuery(id+"F0.wireOp",EDGE,"E0.0.6.37"),sQuery(id+"F0.wireOp",EDGE,"E0.0.6.39"),sQuery(id+"F0.wireOp",EDGE,"E0.0.6.41"),sQuery(id+"F0.wireOp",EDGE,"E0.0.6.44"),sQuery(id+"F0.wireOp",EDGE,"E0.0.6.45"),sQuery(id+"F0.wireOp",EDGE,"E0.0.6.46"),sQuery(id+"F0.wireOp",EDGE,"E0.0.6.47"),sQuery(id+"F0.wireOp",EDGE,"E0.0.6.48"),sQuery(id+"F0.wireOp",EDGE,"E0.0.6.49"),sQuery(id+"F0.wireOp",EDGE,"E0.0.6.50"),sQuery(id+"F0.wireOp",EDGE,"E0.0.6.51"),sQuery(id+"F0.wireOp",EDGE,"E0.0.6.52"),sQuery(id+"F0.wireOp",EDGE,"E0.0.6.53"),sQuery(id+"F0.wireOp",EDGE,"E0.0.6.54"),sQuery(id+"F0.wireOp",EDGE,"E0.0.6.55"),sQuery(id+"F0.wireOp",EDGE,"E0.0.6.56"),sQuery(id+"F0.wireOp",EDGE,"E0.0.6.57"),sQuery(id+"F0.wireOp",EDGE,"E0.0.6.58"),sQuery(id+"F0.wireOp",EDGE,"E0.0.6.59"),sQuery(id+"F0.wireOp",EDGE,"E0.0.6.60"),sQuery(id+"F0.wireOp",EDGE,"E0.0.6.61"),sQuery(id+"F0.wireOp",EDGE,"E0.0.7.0"),sQuery(id+"F0.wireOp",EDGE,"E0.0.7.1"),sQuery(id+"F0.wireOp",EDGE,"E0.0.7.2"),sQuery(id+"F0.wireOp",EDGE,"E0.0.7.3"),sQuery(id+"F0.wireOp",EDGE,"E0.0.7.4"),sQuery(id+"F0.wireOp",EDGE,"E0.0.7.5"),sQuery(id+"F0.wireOp",EDGE,"E0.0.7.6"),sQuery(id+"F0.wireOp",EDGE,"E0.0.7.7"),sQuery(id+"F0.wireOp",EDGE,"E0.0.7.18"),sQuery(id+"F0.wireOp",EDGE,"E0.0.7.19"),sQuery(id+"F0.wireOp",EDGE,"E0.0.7.22"),sQuery(id+"F0.wireOp",EDGE,"E0.0.7.25"),sQuery(id+"F0.wireOp",EDGE,"E0.0.7.32"),sQuery(id+"F0.wireOp",EDGE,"E0.0.7.33"),sQuery(id+"F0.wireOp",EDGE,"E0.0.7.34"),sQuery(id+"F0.wireOp",EDGE,"E0.0.7.35"),sQuery(id+"F0.wireOp",EDGE,"E0.0.7.36"),sQuery(id+"F0.wireOp",EDGE,"E0.0.7.37"),sQuery(id+"F0.wireOp",EDGE,"E0.0.7.39"),sQuery(id+"F0.wireOp",EDGE,"E0.0.7.41"),sQuery(id+"F0.wireOp",EDGE,"E0.0.7.44"),sQuery(id+"F0.wireOp",EDGE,"E0.0.7.45"),sQuery(id+"F0.wireOp",EDGE,"E0.0.7.46"),sQuery(id+"F0.wireOp",EDGE,"E0.0.7.47"),sQuery(id+"F0.wireOp",EDGE,"E0.0.7.48"),sQuery(id+"F0.wireOp",EDGE,"E0.0.7.49"),sQuery(id+"F0.wireOp",EDGE,"E0.0.7.50"),sQuery(id+"F0.wireOp",EDGE,"E0.0.7.51"),sQuery(id+"F0.wireOp",EDGE,"E0.0.7.52"),sQuery(id+"F0.wireOp",EDGE,"E0.0.7.53"),sQuery(id+"F0.wireOp",EDGE,"E0.0.7.54"),sQuery(id+"F0.wireOp",EDGE,"E0.0.7.55"),sQuery(id+"F0.wireOp",EDGE,"E0.0.7.56"),sQuery(id+"F0.wireOp",EDGE,"E0.0.7.57"),sQuery(id+"F0.wireOp",EDGE,"E0.0.7.58"),sQuery(id+"F0.wireOp",EDGE,"E0.0.7.59"),sQuery(id+"F0.wireOp",EDGE,"E0.0.7.60"),sQuery(id+"F0.wireOp",EDGE,"E0.0.7.61"),sQuery(id+"F0.wireOp",EDGE,"E1.1.0.161"),sQuery(id+"F0.wireOp",EDGE,"E1.1.0.162"),sQuery(id+"F0.wireOp",EDGE,"E1.1.0.163"),sQuery(id+"F0.wireOp",EDGE,"E1.1.0.166"),sQuery(id+"F0.wireOp",EDGE,"E1.1.0.171"),sQuery(id+"F0.wireOp",EDGE,"E1.1.0.173"),sQuery(id+"F0.wireOp",EDGE,"E1.1.0.174"),sQuery(id+"F0.wireOp",EDGE,"E1.1.0.175"),sQuery(id+"F0.wireOp",EDGE,"E1.1.0.176"),sQuery(id+"F0.wireOp",EDGE,"E1.1.0.177"),sQuery(id+"F0.wireOp",EDGE,"E1.1.0.180"),sQuery(id+"F0.wireOp",EDGE,"E1.1.0.185"),sQuery(id+"F0.wireOp",EDGE,"E1.1.0.194"),sQuery(id+"F0.wireOp",EDGE,"E1.1.0.205"),sQuery(id+"F0.wireOp",EDGE,"E1.1.0.215"),sQuery(id+"F0.wireOp",EDGE,"E1.1.0.216"),sQuery(id+"F0.wireOp",EDGE,"E1.1.0.218"),sQuery(id+"F0.wireOp",EDGE,"E1.1.0.222"),sQuery(id+"F0.wireOp",EDGE,"E1.1.0.228"),sQuery(id+"F0.wireOp",EDGE,"E1.1.0.229"),sQuery(id+"F0.wireOp",EDGE,"E1.1.0.230"),sQuery(id+"F0.wireOp",EDGE,"E1.1.0.231"),sQuery(id+"F0.wireOp",EDGE,"E1.1.0.239"),sQuery(id+"F0.wireOp",EDGE,"E1.1.0.240"),sQuery(id+"F0.wireOp",EDGE,"E1.1.0.242"),sQuery(id+"F0.wireOp",EDGE,"E1.1.0.243"),sQuery(id+"F0.wireOp",EDGE,"E1.1.0.244"),sQuery(id+"F0.wireOp",EDGE,"E1.1.0.246"),sQuery(id+"F0.wireOp",EDGE,"E1.1.0.249"),sQuery(id+"F0.wireOp",EDGE,"E1.1.0.250"),sQuery(id+"F0.wireOp",EDGE,"E1.1.0.251"),sQuery(id+"F0.wireOp",EDGE,"E1.1.0.253"),sQuery(id+"F0.wireOp",EDGE,"E1.1.0.257"),sQuery(id+"F0.wireOp",EDGE,"E1.1.0.259"),sQuery(id+"F0.wireOp",EDGE,"E1.1.0.260"),sQuery(id+"F0.wireOp",EDGE,"E1.1.0.264"),sQuery(id+"F0.wireOp",EDGE,"E1.1.0.265"),sQuery(id+"F0.wireOp",EDGE,"E1.1.0.266"),sQuery(id+"F0.wireOp",EDGE,"E1.1.0.269"),sQuery(id+"F0.wireOp",EDGE,"E1.1.0.274"),sQuery(id+"F0.wireOp",EDGE,"E1.1.0.275"),sQuery(id+"F0.wireOp",EDGE,"E1.1.0.276"),sQuery(id+"F0.wireOp",EDGE,"E1.1.0.278"),sQuery(id+"F0.wireOp",EDGE,"E1.1.0.280"),sQuery(id+"F0.wireOp",EDGE,"E1.1.0.284"),sQuery(id+"F0.wireOp",EDGE,"E1.1.0.285"),sQuery(id+"F0.wireOp",EDGE,"E1.1.0.288"),sQuery(id+"F0.wireOp",EDGE,"E1.1.0.289"),sQuery(id+"F0.wireOp",EDGE,"E1.1.0.290"),sQuery(id+"F0.wireOp",EDGE,"E1.1.0.292"),sQuery(id+"F0.wireOp",EDGE,"E1.1.0.293"),sQuery(id+"F0.wireOp",EDGE,"E1.1.0.295"),sQuery(id+"F0.wireOp",EDGE,"E1.1.0.298"),sQuery(id+"F0.wireOp",EDGE,"E1.1.0.299"),sQuery(id+"F0.wireOp",EDGE,"E1.1.0.301"),sQuery(id+"F0.wireOp",EDGE,"E1.1.0.304"),sQuery(id+"F0.wireOp",EDGE,"E1.1.0.305"),sQuery(id+"F0.wireOp",EDGE,"E1.1.0.308"),sQuery(id+"F0.wireOp",EDGE,"E1.1.0.311"),sQuery(id+"F0.wireOp",EDGE,"E1.1.0.312"),sQuery(id+"F0.wireOp",EDGE,"E1.1.0.315"),sQuery(id+"F0.wireOp",EDGE,"E1.1.0.316"),sQuery(id+"F0.wireOp",EDGE,"E1.1.0.317"),sQuery(id+"F0.wireOp",EDGE,"E1.1.0.326"),sQuery(id+"F0.wireOp",EDGE,"E1.1.0.327"),sQuery(id+"F0.wireOp",EDGE,"E1.1.0.328"),sQuery(id+"F0.wireOp",EDGE,"E1.1.0.333"),sQuery(id+"F0.wireOp",EDGE,"E1.1.0.337"),sQuery(id+"F0.wireOp",EDGE,"E1.1.0.340"),sQuery(id+"F0.wireOp",EDGE,"E1.1.0.343"),sQuery(id+"F0.wireOp",EDGE,"E1.1.0.345"),sQuery(id+"F0.wireOp",EDGE,"E1.1.0.349"),sQuery(id+"F0.wireOp",EDGE,"E1.1.0.356"),sQuery(id+"F0.wireOp",EDGE,"E1.1.0.357"),sQuery(id+"F0.wireOp",EDGE,"E1.1.0.363"),sQuery(id+"F0.wireOp",EDGE,"E1.1.0.369"),sQuery(id+"F0.wireOp",EDGE,"E1.1.0.371"),sQuery(id+"F0.wireOp",EDGE,"E1.1.0.374"),sQuery(id+"F0.wireOp",EDGE,"E1.1.0.375"),sQuery(id+"F0.wireOp",EDGE,"E1.1.0.377"),sQuery(id+"F0.wireOp",EDGE,"E1.1.0.382"),sQuery(id+"F0.wireOp",EDGE,"E1.1.0.383"),sQuery(id+"F0.wireOp",EDGE,"E1.1.0.385"),sQuery(id+"F0.wireOp",EDGE,"E1.1.0.386"),sQuery(id+"F0.wireOp",EDGE,"E1.1.0.390"),sQuery(id+"F0.wireOp",EDGE,"E1.1.0.397"),sQuery(id+"F0.wireOp",EDGE,"E1.1.0.399"),sQuery(id+"F0.wireOp",EDGE,"E1.1.0.402"),sQuery(id+"F0.wireOp",EDGE,"E1.1.0.403"),sQuery(id+"F0.wireOp",EDGE,"E1.1.0.410"),sQuery(id+"F0.wireOp",EDGE,"E1.1.0.418"),sQuery(id+"F0.wireOp",EDGE,"E1.1.0.421"),sQuery(id+"F0.wireOp",EDGE,"E1.1.0.423"),sQuery(id+"F0.wireOp",EDGE,"E1.1.0.426"),sQuery(id+"F0.wireOp",EDGE,"E1.1.0.430"),sQuery(id+"F0.wireOp",EDGE,"E1.1.0.432"),sQuery(id+"F0.wireOp",EDGE,"E1.2.0.161"),sQuery(id+"F0.wireOp",EDGE,"E1.2.0.162"),sQuery(id+"F0.wireOp",EDGE,"E1.2.0.163"),sQuery(id+"F0.wireOp",EDGE,"E1.2.0.166"),sQuery(id+"F0.wireOp",EDGE,"E1.2.0.171"),sQuery(id+"F0.wireOp",EDGE,"E1.2.0.173"),sQuery(id+"F0.wireOp",EDGE,"E1.2.0.174"),sQuery(id+"F0.wireOp",EDGE,"E1.2.0.175"),sQuery(id+"F0.wireOp",EDGE,"E1.2.0.176"),sQuery(id+"F0.wireOp",EDGE,"E1.2.0.177"),sQuery(id+"F0.wireOp",EDGE,"E1.2.0.180"),sQuery(id+"F0.wireOp",EDGE,"E1.2.0.185"),sQuery(id+"F0.wireOp",EDGE,"E1.2.0.194"),sQuery(id+"F0.wireOp",EDGE,"E1.2.0.205"),sQuery(id+"F0.wireOp",EDGE,"E1.2.0.215"),sQuery(id+"F0.wireOp",EDGE,"E1.2.0.216"),sQuery(id+"F0.wireOp",EDGE,"E1.2.0.218"),sQuery(id+"F0.wireOp",EDGE,"E1.2.0.222"),sQuery(id+"F0.wireOp",EDGE,"E1.2.0.228"),sQuery(id+"F0.wireOp",EDGE,"E1.2.0.229"),sQuery(id+"F0.wireOp",EDGE,"E1.2.0.230"),sQuery(id+"F0.wireOp",EDGE,"E1.2.0.231"),sQuery(id+"F0.wireOp",EDGE,"E1.2.0.239"),sQuery(id+"F0.wireOp",EDGE,"E1.2.0.240"),sQuery(id+"F0.wireOp",EDGE,"E1.2.0.242"),sQuery(id+"F0.wireOp",EDGE,"E1.2.0.243"),sQuery(id+"F0.wireOp",EDGE,"E1.2.0.244"),sQuery(id+"F0.wireOp",EDGE,"E1.2.0.246"),sQuery(id+"F0.wireOp",EDGE,"E1.2.0.249"),sQuery(id+"F0.wireOp",EDGE,"E1.2.0.250"),sQuery(id+"F0.wireOp",EDGE,"E1.2.0.251"),sQuery(id+"F0.wireOp",EDGE,"E1.2.0.253"),sQuery(id+"F0.wireOp",EDGE,"E1.2.0.257"),sQuery(id+"F0.wireOp",EDGE,"E1.2.0.259"),sQuery(id+"F0.wireOp",EDGE,"E1.2.0.260"),sQuery(id+"F0.wireOp",EDGE,"E1.2.0.264"),sQuery(id+"F0.wireOp",EDGE,"E1.2.0.265"),sQuery(id+"F0.wireOp",EDGE,"E1.2.0.266"),sQuery(id+"F0.wireOp",EDGE,"E1.2.0.269"),sQuery(id+"F0.wireOp",EDGE,"E1.2.0.274"),sQuery(id+"F0.wireOp",EDGE,"E1.2.0.275"),sQuery(id+"F0.wireOp",EDGE,"E1.2.0.276"),sQuery(id+"F0.wireOp",EDGE,"E1.2.0.278"),sQuery(id+"F0.wireOp",EDGE,"E1.2.0.280"),sQuery(id+"F0.wireOp",EDGE,"E1.2.0.284"),sQuery(id+"F0.wireOp",EDGE,"E1.2.0.285"),sQuery(id+"F0.wireOp",EDGE,"E1.2.0.288"),sQuery(id+"F0.wireOp",EDGE,"E1.2.0.289"),sQuery(id+"F0.wireOp",EDGE,"E1.2.0.290"),sQuery(id+"F0.wireOp",EDGE,"E1.2.0.292"),sQuery(id+"F0.wireOp",EDGE,"E1.2.0.293"),sQuery(id+"F0.wireOp",EDGE,"E1.2.0.295"),sQuery(id+"F0.wireOp",EDGE,"E1.2.0.298"),sQuery(id+"F0.wireOp",EDGE,"E1.2.0.299"),sQuery(id+"F0.wireOp",EDGE,"E1.2.0.301"),sQuery(id+"F0.wireOp",EDGE,"E1.2.0.304"),sQuery(id+"F0.wireOp",EDGE,"E1.2.0.305"),sQuery(id+"F0.wireOp",EDGE,"E1.2.0.308"),sQuery(id+"F0.wireOp",EDGE,"E1.2.0.311"),sQuery(id+"F0.wireOp",EDGE,"E1.2.0.312"),sQuery(id+"F0.wireOp",EDGE,"E1.2.0.315"),sQuery(id+"F0.wireOp",EDGE,"E1.2.0.316"),sQuery(id+"F0.wireOp",EDGE,"E1.2.0.317"),sQuery(id+"F0.wireOp",EDGE,"E1.2.0.326"),sQuery(id+"F0.wireOp",EDGE,"E1.2.0.327"),sQuery(id+"F0.wireOp",EDGE,"E1.2.0.328"),sQuery(id+"F0.wireOp",EDGE,"E1.2.0.333"),sQuery(id+"F0.wireOp",EDGE,"E1.2.0.337"),sQuery(id+"F0.wireOp",EDGE,"E1.2.0.340"),sQuery(id+"F0.wireOp",EDGE,"E1.2.0.343"),sQuery(id+"F0.wireOp",EDGE,"E1.2.0.345"),sQuery(id+"F0.wireOp",EDGE,"E1.2.0.349"),sQuery(id+"F0.wireOp",EDGE,"E1.2.0.356"),sQuery(id+"F0.wireOp",EDGE,"E1.2.0.357"),sQuery(id+"F0.wireOp",EDGE,"E1.2.0.363"),sQuery(id+"F0.wireOp",EDGE,"E1.2.0.369"),sQuery(id+"F0.wireOp",EDGE,"E1.2.0.371"),sQuery(id+"F0.wireOp",EDGE,"E1.2.0.374"),sQuery(id+"F0.wireOp",EDGE,"E1.2.0.375"),sQuery(id+"F0.wireOp",EDGE,"E1.2.0.377"),sQuery(id+"F0.wireOp",EDGE,"E1.2.0.382"),sQuery(id+"F0.wireOp",EDGE,"E1.2.0.383"),sQuery(id+"F0.wireOp",EDGE,"E1.2.0.385"),sQuery(id+"F0.wireOp",EDGE,"E1.2.0.386"),sQuery(id+"F0.wireOp",EDGE,"E1.2.0.390"),sQuery(id+"F0.wireOp",EDGE,"E1.2.0.397"),sQuery(id+"F0.wireOp",EDGE,"E1.2.0.399"),sQuery(id+"F0.wireOp",EDGE,"E1.2.0.402"),sQuery(id+"F0.wireOp",EDGE,"E1.2.0.403"),sQuery(id+"F0.wireOp",EDGE,"E1.2.0.410"),sQuery(id+"F0.wireOp",EDGE,"E1.2.0.418"),sQuery(id+"F0.wireOp",EDGE,"E1.2.0.421"),sQuery(id+"F0.wireOp",EDGE,"E1.2.0.423"),sQuery(id+"F0.wireOp",EDGE,"E1.2.0.426"),sQuery(id+"F0.wireOp",EDGE,"E1.2.0.430"),sQuery(id+"F0.wireOp",EDGE,"E1.2.0.432"),sQuery(id+"F0.wireOp",EDGE,"E2.163.3.0"),sQuery(id+"F0.wireOp",EDGE,"E2.166.3.0"),sQuery(id+"F0.wireOp",EDGE,"E2.169.3.0"),sQuery(id+"F0.wireOp",EDGE,"E2.178.3.0"),sQuery(id+"F0.wireOp",EDGE,"E2.193.3.0"),sQuery(id+"F0.wireOp",EDGE,"E2.199.3.0"),sQuery(id+"F0.wireOp",EDGE,"E2.202.3.0"),sQuery(id+"F0.wireOp",EDGE,"E2.205.3.0"),sQuery(id+"F0.wireOp",EDGE,"E2.209.3.0"),sQuery(id+"F0.wireOp",EDGE,"E2.212.3.0"),sQuery(id+"F0.wireOp",EDGE,"E2.221.3.0"),sQuery(id+"F0.wireOp",EDGE,"E2.263.3.0"),sQuery(id+"F0.wireOp",EDGE,"E2.328.3.0"),sQuery(id+"F0.wireOp",EDGE,"E2.332.3.0"),sQuery(id+"F0.wireOp",EDGE,"E2.370.3.0"),sQuery(id+"F0.wireOp",EDGE,"E2.373.3.0"),sQuery(id+"F0.wireOp",EDGE,"E2.379.3.0"),sQuery(id+"F0.wireOp",EDGE,"E2.404.3.0"),sQuery(id+"F0.wireOp",EDGE,"E2.413.3.0"),sQuery(id+"F0.wireOp",EDGE,"E2.416.3.0"),sQuery(id+"F0.wireOp",EDGE,"E2.420.3.0"),sQuery(id+"F0.wireOp",EDGE,"E2.437.3.0"),sQuery(id+"F0.wireOp",EDGE,"E2.440.3.0"),sQuery(id+"F0.wireOp",EDGE,"E2.443.3.0"),sQuery(id+"F0.wireOp",EDGE,"E2.463.3.0"),sQuery(id+"F0.wireOp",EDGE,"E2.469.3.0"),sQuery(id+"F0.wireOp",EDGE,"E2.472.3.0"),sQuery(id+"F0.wireOp",EDGE,"E2.485.3.0"),sQuery(id+"F0.wireOp",EDGE,"E2.502.3.0"),sQuery(id+"F0.wireOp",EDGE,"E2.520.3.0"),sQuery(id+"F0.wireOp",EDGE,"E2.530.3.0"),sQuery(id+"F0.wireOp",EDGE,"E2.554.3.0"),sQuery(id+"F0.wireOp",EDGE,"E2.564.3.0"),sQuery(id+"F0.wireOp",EDGE,"E2.567.3.0"),sQuery(id+"F0.wireOp",EDGE,"E2.571.3.0"),sQuery(id+"F0.wireOp",EDGE,"E2.577.3.0"),sQuery(id+"F0.wireOp",EDGE,"E2.580.3.0"),sQuery(id+"F0.wireOp",EDGE,"E2.586.3.0"),sQuery(id+"F0.wireOp",EDGE,"E2.596.3.0"),sQuery(id+"F0.wireOp",EDGE,"E2.600.3.0"),sQuery(id+"F0.wireOp",EDGE,"E2.607.3.0"),sQuery(id+"F0.wireOp",EDGE,"E2.618.3.0"),sQuery(id+"F0.wireOp",EDGE,"E2.622.3.0"),sQuery(id+"F0.wireOp",EDGE,"E2.645.3.0"),sQuery(id+"F0.wireOp",EDGE,"E2.648.3.0"),sQuery(id+"F0.wireOp",EDGE,"E2.658.3.0"),sQuery(id+"F0.wireOp",EDGE,"E2.665.3.0"),sQuery(id+"F0.wireOp",EDGE,"E2.693.3.0"),sQuery(id+"F0.wireOp",EDGE,"E2.696.3.0"),sQuery(id+"F0.wireOp",EDGE,"E2.699.3.0"),sQuery(id+"F0.wireOp",EDGE,"E2.715.3.0"),sQuery(id+"F0.wireOp",EDGE,"E2.730.3.0"),sQuery(id+"F0.wireOp",EDGE,"E2.742.3.0"),sQuery(id+"F0.wireOp",EDGE,"E2.751.3.0"),sQuery(id+"F0.wireOp",EDGE,"E2.758.3.0"),sQuery(id+"F0.wireOp",EDGE,"E2.773.3.0"),sQuery(id+"F0.wireOp",EDGE,"E2.799.3.0"),sQuery(id+"F0.wireOp",EDGE,"E2.803.3.0"),sQuery(id+"F0.wireOp",EDGE,"E2.825.3.0"),sQuery(id+"F0.wireOp",EDGE,"E2.848.3.0"),sQuery(id+"F0.wireOp",EDGE,"E2.855.3.0"),sQuery(id+"F0.wireOp",EDGE,"E2.866.3.0"),sQuery(id+"F0.wireOp",EDGE,"E2.870.3.0"),sQuery(id+"F0.wireOp",EDGE,"E2.877.3.0"),sQuery(id+"F0.wireOp",EDGE,"E2.894.3.0"),sQuery(id+"F0.wireOp",EDGE,"E2.904.3.0"),sQuery(id+"F0.wireOp",EDGE,"E2.907.3.0"),sQuery(id+"F0.wireOp",EDGE,"E2.922.3.0"),sQuery(id+"F0.wireOp",EDGE,"E2.947.3.0"),sQuery(id+"F0.wireOp",EDGE,"E2.965.3.0"),sQuery(id+"F0.wireOp",EDGE,"E2.992.3.0"),sQuery(id+"F0.wireOp",EDGE,"E2.1020.3.0"),sQuery(id+"F0.wireOp",EDGE,"E2.1038.3.0"),sQuery(id+"F0.wireOp",EDGE,"E2.1049.3.0"),sQuery(id+"F0.wireOp",EDGE,"E2.1063.3.0"),sQuery(id+"F0.wireOp",EDGE,"E2.1070.3.0"),sQuery(id+"F0.wireOp",EDGE,"E3"),sQuery(id+"F0.wireOp",EDGE,"E4"),sQuery(id+"F0.wireOp",EDGE,"E5"),sQuery(id+"F0.wireOp",EDGE,"E6"),sQuery(id+"F0.wireOp",EDGE,"E7"),sQuery(id+"F0.wireOp",EDGE,"E8"),sQuery(id+"F0.wireOp",EDGE,"E9"),sQuery(id+"F0.wireOp",EDGE,"E10"),sQuery(id+"F0.wireOp",EDGE,"E11"),sQuery(id+"F0.wireOp",EDGE,"E12"),sQuery(id+"F0.wireOp",EDGE,"E13"),sQuery(id+"F0.wireOp",EDGE,"E14"),sQuery(id+"F0.wireOp",EDGE,"E15"),sQuery(id+"F0.wireOp",EDGE,"E16"),sQuery(id+"F0.wireOp",EDGE,"E17"),sQuery(id+"F0.wireOp",EDGE,"E18"),sQuery(id+"F0.wireOp",EDGE,"E19"),sQuery(id+"F0.wireOp",EDGE,"E20"),sQuery(id+"F0.wireOp",EDGE,"E21"),sQuery(id+"F0.wireOp",EDGE,"E22"),sQuery(id+"F0.wireOp",EDGE,"E23"),sQuery(id+"F0.wireOp",EDGE,"E24"),sQuery(id+"F0.wireOp",EDGE,"E25"),sQuery(id+"F0.wireOp",EDGE,"E26"),sQuery(id+"F0.wireOp",EDGE,"E27"),sQuery(id+"F0.wireOp",EDGE,"E28"),sQuery(id+"F0.wireOp",EDGE,"E29"),sQuery(id+"F0.wireOp",EDGE,"E30"),sQuery(id+"F0.wireOp",EDGE,"E31"),sQuery(id+"F0.wireOp",EDGE,"E32"),sQuery(id+"F0.wireOp",EDGE,"E33"),sQuery(id+"F0.wireOp",EDGE,"E34"),sQuery(id+"F0.wireOp",EDGE,"E35"),sQuery(id+"F0.wireOp",EDGE,"E36"),sQuery(id+"F0.wireOp",EDGE,"E37"),sQuery(id+"F0.wireOp",EDGE,"E38"),sQuery(id+"F0.wireOp",EDGE,"E39"),sQuery(id+"F0.wireOp",EDGE,"E40"),sQuery(id+"F0.wireOp",EDGE,"E41"),sQuery(id+"F0.wireOp",EDGE,"E42"),sQuery(id+"F0.wireOp",EDGE,"E43"),sQuery(id+"F0.wireOp",EDGE,"E44"),sQuery(id+"F0.wireOp",EDGE,"E45"),sQuery(id+"F0.wireOp",EDGE,"E46"),sQuery(id+"F0.wireOp",EDGE,"E47"),sQuery(id+"F0.wireOp",EDGE,"E48"),sQuery(id+"F0.wireOp",EDGE,"E49"),sQuery(id+"F0.wireOp",EDGE,"E50"),sQuery(id+"F0.wireOp",EDGE,"E51"),sQuery(id+"F0.wireOp",EDGE,"E52.filletArc"),sQuery(id+"F0.wireOp",EDGE,"E53.filletArc"),sQuery(id+"F0.wireOp",EDGE,"E54.filletArc"),sQuery(id+"F0.wireOp",EDGE,"E55.filletArc"),sQuery(id+"F0.wireOp",EDGE,"E56.filletArc"),sQuery(id+"F0.wireOp",EDGE,"E57.filletArc"),sQuery(id+"F0.wireOp",EDGE,"E58.filletArc"),sQuery(id+"F0.wireOp",EDGE,"E59.filletArc"),sQuery(id+"F0.wireOp",EDGE,"E60.trimOffspring"),sQuery(id+"F0.wireOp",EDGE,"E61.filletArc"),sQuery(id+"F0.wireOp",EDGE,"E62.filletArc")])],"isStart":false});
            var sketch = newSketch(context, id + "F2", { "sketchPlane" : qUnion([Q0])});
            skLineSegment(sketch, "E106.bottom", {"start": v(46.64, 31.64) * mm, "end": v(43.68, 31.64) * mm});
            skLineSegment(sketch, "E106.top", {"start": v(46.64, 27.4) * mm, "end": v(43.68, 27.4) * mm});
            skLineSegment(sketch, "E106.left", {"start": v(46.64, 31.64) * mm, "end": v(46.64, 27.4) * mm});
            skLineSegment(sketch, "E106.right", {"start": v(42.62, 30.59) * mm, "end": v(42.62, 28.45) * mm});
            skPoint(sketch, "E107.visualSharp", {"position": v(42.62, 31.64) * mm});
            skArc(sketch, "E107.filletArc", {"start": v(43.68, 31.64) * mm, "mid": v(42.93, 31.33) * mm, "end": v(42.62, 30.59) * mm});
            skPoint(sketch, "E108.visualSharp", {"position": v(42.62, 27.4) * mm});
            skArc(sketch, "E108.filletArc", {"start": v(42.62, 28.45) * mm, "mid": v(42.93, 27.7) * mm, "end": v(43.68, 27.4) * mm});
            skSolve(sketch);
        }
        {
            var Q0;
            {var subQ4=makeQuery(id+"F1.opExtrude","CAP_EDGE",EDGE,{"disambiguationData":[OSD([sQuery(id+"F0.wireOp",EDGE,"E51")])],"isStart":false});Q0=makeQuery(id+"F2.imprint","IMPRINT",FACE,{"disambiguationData":[TD([[makeQuery(id+"F2.imprint","IMPRINT",EDGE,{"derivedFrom":subQ4}),-1.0]])]});}
            extrude(context, id + "F3", {"entities" : qUnion([Q0]), "operationType" : NewBodyOperationType.ADD, "depth" : .5 * mm, "offsetDistance" : 25 * mm});
        }
        {
            var Q0;
            Q0=makeQuery(id+"F3.opExtrude","CAP_FACE",FACE,{"disambiguationData":[OSD([sQuery(id+"F0.wireOp",EDGE,"E51"),sQuery(id+"F0.wireOp",EDGE,"E52.filletArc"),sQuery(id+"F0.wireOp",EDGE,"E53.filletArc"),sQuery(id+"F2.wireOp",EDGE,"E106.bottom"),sQuery(id+"F2.wireOp",EDGE,"E106.top"),sQuery(id+"F2.wireOp",EDGE,"E106.left")])],"isStart":false});
            var sketch = newSketch(context, id + "F4", { "sketchPlane" : qUnion([Q0])});
            skLineSegment(sketch, "E109.bottom", {"start": v(46.36, 31.29) * mm, "end": v(44, 31.29) * mm});
            skLineSegment(sketch, "E109.top", {"start": v(46.36, 27.68) * mm, "end": v(44, 27.68) * mm});
            skLineSegment(sketch, "E109.left", {"start": v(46.36, 31.29) * mm, "end": v(46.36, 27.68) * mm});
            skLineSegment(sketch, "E109.right", {"start": v(43.03, 30.33) * mm, "end": v(43.03, 28.64) * mm});
            skPoint(sketch, "E110.visualSharp", {"position": v(43.03, 31.29) * mm});
            skArc(sketch, "E110.filletArc", {"start": v(44, 31.29) * mm, "mid": v(43.31, 31) * mm, "end": v(43.03, 30.33) * mm});
            skPoint(sketch, "E111.visualSharp", {"position": v(43.03, 27.68) * mm});
            skArc(sketch, "E111.filletArc", {"start": v(43.03, 28.64) * mm, "mid": v(43.31, 27.96) * mm, "end": v(44, 27.68) * mm});
            skSolve(sketch);
        }
        {
            var Q0;
            Q0=qSketchRegion(id+"F4",true);
            extrude(context, id + "F5", {"entities" : qUnion([Q0]), "operationType" : NewBodyOperationType.REMOVE, "depth" : -.5 * mm, "offsetDistance" : 25 * mm});
        }
        {
            var Q0;
            Q0=makeQuery(id+"F1.opExtrude","CAP_FACE",FACE,{"disambiguationData":[OSD([sQuery(id+"F0.wireOp",EDGE,"E0.0.5.4"),sQuery(id+"F0.wireOp",EDGE,"E0.0.5.5"),sQuery(id+"F0.wireOp",EDGE,"E0.0.5.6"),sQuery(id+"F0.wireOp",EDGE,"E0.0.5.7"),sQuery(id+"F0.wireOp",EDGE,"E0.0.5.18"),sQuery(id+"F0.wireOp",EDGE,"E0.0.5.19"),sQuery(id+"F0.wireOp",EDGE,"E0.0.5.32"),sQuery(id+"F0.wireOp",EDGE,"E0.0.5.33"),sQuery(id+"F0.wireOp",EDGE,"E0.0.5.34"),sQuery(id+"F0.wireOp",EDGE,"E0.0.5.41"),sQuery(id+"F0.wireOp",EDGE,"E0.0.5.44"),sQuery(id+"F0.wireOp",EDGE,"E0.0.5.45"),sQuery(id+"F0.wireOp",EDGE,"E0.0.5.46"),sQuery(id+"F0.wireOp",EDGE,"E0.0.5.49"),sQuery(id+"F0.wireOp",EDGE,"E0.0.5.50"),sQuery(id+"F0.wireOp",EDGE,"E0.0.5.55"),sQuery(id+"F0.wireOp",EDGE,"E0.0.5.56"),sQuery(id+"F0.wireOp",EDGE,"E0.0.5.57"),sQuery(id+"F0.wireOp",EDGE,"E0.0.5.60"),sQuery(id+"F0.wireOp",EDGE,"E0.0.5.61"),sQuery(id+"F0.wireOp",EDGE,"E0.0.6.0"),sQuery(id+"F0.wireOp",EDGE,"E0.0.6.1"),sQuery(id+"F0.wireOp",EDGE,"E0.0.6.2"),sQuery(id+"F0.wireOp",EDGE,"E0.0.6.3"),sQuery(id+"F0.wireOp",EDGE,"E0.0.6.4"),sQuery(id+"F0.wireOp",EDGE,"E0.0.6.5"),sQuery(id+"F0.wireOp",EDGE,"E0.0.6.6"),sQuery(id+"F0.wireOp",EDGE,"E0.0.6.7"),sQuery(id+"F0.wireOp",EDGE,"E0.0.6.18"),sQuery(id+"F0.wireOp",EDGE,"E0.0.6.19"),sQuery(id+"F0.wireOp",EDGE,"E0.0.6.22"),sQuery(id+"F0.wireOp",EDGE,"E0.0.6.25"),sQuery(id+"F0.wireOp",EDGE,"E0.0.6.32"),sQuery(id+"F0.wireOp",EDGE,"E0.0.6.33"),sQuery(id+"F0.wireOp",EDGE,"E0.0.6.34"),sQuery(id+"F0.wireOp",EDGE,"E0.0.6.35"),sQuery(id+"F0.wireOp",EDGE,"E0.0.6.36"),sQuery(id+"F0.wireOp",EDGE,"E0.0.6.37"),sQuery(id+"F0.wireOp",EDGE,"E0.0.6.39"),sQuery(id+"F0.wireOp",EDGE,"E0.0.6.41"),sQuery(id+"F0.wireOp",EDGE,"E0.0.6.44"),sQuery(id+"F0.wireOp",EDGE,"E0.0.6.45"),sQuery(id+"F0.wireOp",EDGE,"E0.0.6.46"),sQuery(id+"F0.wireOp",EDGE,"E0.0.6.47"),sQuery(id+"F0.wireOp",EDGE,"E0.0.6.48"),sQuery(id+"F0.wireOp",EDGE,"E0.0.6.49"),sQuery(id+"F0.wireOp",EDGE,"E0.0.6.50"),sQuery(id+"F0.wireOp",EDGE,"E0.0.6.51"),sQuery(id+"F0.wireOp",EDGE,"E0.0.6.52"),sQuery(id+"F0.wireOp",EDGE,"E0.0.6.53"),sQuery(id+"F0.wireOp",EDGE,"E0.0.6.54"),sQuery(id+"F0.wireOp",EDGE,"E0.0.6.55"),sQuery(id+"F0.wireOp",EDGE,"E0.0.6.56"),sQuery(id+"F0.wireOp",EDGE,"E0.0.6.57"),sQuery(id+"F0.wireOp",EDGE,"E0.0.6.58"),sQuery(id+"F0.wireOp",EDGE,"E0.0.6.59"),sQuery(id+"F0.wireOp",EDGE,"E0.0.6.60"),sQuery(id+"F0.wireOp",EDGE,"E0.0.6.61"),sQuery(id+"F0.wireOp",EDGE,"E0.0.7.0"),sQuery(id+"F0.wireOp",EDGE,"E0.0.7.1"),sQuery(id+"F0.wireOp",EDGE,"E0.0.7.2"),sQuery(id+"F0.wireOp",EDGE,"E0.0.7.3"),sQuery(id+"F0.wireOp",EDGE,"E0.0.7.4"),sQuery(id+"F0.wireOp",EDGE,"E0.0.7.5"),sQuery(id+"F0.wireOp",EDGE,"E0.0.7.6"),sQuery(id+"F0.wireOp",EDGE,"E0.0.7.7"),sQuery(id+"F0.wireOp",EDGE,"E0.0.7.18"),sQuery(id+"F0.wireOp",EDGE,"E0.0.7.19"),sQuery(id+"F0.wireOp",EDGE,"E0.0.7.22"),sQuery(id+"F0.wireOp",EDGE,"E0.0.7.25"),sQuery(id+"F0.wireOp",EDGE,"E0.0.7.32"),sQuery(id+"F0.wireOp",EDGE,"E0.0.7.33"),sQuery(id+"F0.wireOp",EDGE,"E0.0.7.34"),sQuery(id+"F0.wireOp",EDGE,"E0.0.7.35"),sQuery(id+"F0.wireOp",EDGE,"E0.0.7.36"),sQuery(id+"F0.wireOp",EDGE,"E0.0.7.37"),sQuery(id+"F0.wireOp",EDGE,"E0.0.7.39"),sQuery(id+"F0.wireOp",EDGE,"E0.0.7.41"),sQuery(id+"F0.wireOp",EDGE,"E0.0.7.44"),sQuery(id+"F0.wireOp",EDGE,"E0.0.7.45"),sQuery(id+"F0.wireOp",EDGE,"E0.0.7.46"),sQuery(id+"F0.wireOp",EDGE,"E0.0.7.47"),sQuery(id+"F0.wireOp",EDGE,"E0.0.7.48"),sQuery(id+"F0.wireOp",EDGE,"E0.0.7.49"),sQuery(id+"F0.wireOp",EDGE,"E0.0.7.50"),sQuery(id+"F0.wireOp",EDGE,"E0.0.7.51"),sQuery(id+"F0.wireOp",EDGE,"E0.0.7.52"),sQuery(id+"F0.wireOp",EDGE,"E0.0.7.53"),sQuery(id+"F0.wireOp",EDGE,"E0.0.7.54"),sQuery(id+"F0.wireOp",EDGE,"E0.0.7.55"),sQuery(id+"F0.wireOp",EDGE,"E0.0.7.56"),sQuery(id+"F0.wireOp",EDGE,"E0.0.7.57"),sQuery(id+"F0.wireOp",EDGE,"E0.0.7.58"),sQuery(id+"F0.wireOp",EDGE,"E0.0.7.59"),sQuery(id+"F0.wireOp",EDGE,"E0.0.7.60"),sQuery(id+"F0.wireOp",EDGE,"E0.0.7.61"),sQuery(id+"F0.wireOp",EDGE,"E1.1.0.161"),sQuery(id+"F0.wireOp",EDGE,"E1.1.0.162"),sQuery(id+"F0.wireOp",EDGE,"E1.1.0.163"),sQuery(id+"F0.wireOp",EDGE,"E1.1.0.166"),sQuery(id+"F0.wireOp",EDGE,"E1.1.0.171"),sQuery(id+"F0.wireOp",EDGE,"E1.1.0.173"),sQuery(id+"F0.wireOp",EDGE,"E1.1.0.174"),sQuery(id+"F0.wireOp",EDGE,"E1.1.0.175"),sQuery(id+"F0.wireOp",EDGE,"E1.1.0.176"),sQuery(id+"F0.wireOp",EDGE,"E1.1.0.177"),sQuery(id+"F0.wireOp",EDGE,"E1.1.0.180"),sQuery(id+"F0.wireOp",EDGE,"E1.1.0.185"),sQuery(id+"F0.wireOp",EDGE,"E1.1.0.194"),sQuery(id+"F0.wireOp",EDGE,"E1.1.0.205"),sQuery(id+"F0.wireOp",EDGE,"E1.1.0.215"),sQuery(id+"F0.wireOp",EDGE,"E1.1.0.216"),sQuery(id+"F0.wireOp",EDGE,"E1.1.0.218"),sQuery(id+"F0.wireOp",EDGE,"E1.1.0.222"),sQuery(id+"F0.wireOp",EDGE,"E1.1.0.228"),sQuery(id+"F0.wireOp",EDGE,"E1.1.0.229"),sQuery(id+"F0.wireOp",EDGE,"E1.1.0.230"),sQuery(id+"F0.wireOp",EDGE,"E1.1.0.231"),sQuery(id+"F0.wireOp",EDGE,"E1.1.0.239"),sQuery(id+"F0.wireOp",EDGE,"E1.1.0.240"),sQuery(id+"F0.wireOp",EDGE,"E1.1.0.242"),sQuery(id+"F0.wireOp",EDGE,"E1.1.0.243"),sQuery(id+"F0.wireOp",EDGE,"E1.1.0.244"),sQuery(id+"F0.wireOp",EDGE,"E1.1.0.246"),sQuery(id+"F0.wireOp",EDGE,"E1.1.0.249"),sQuery(id+"F0.wireOp",EDGE,"E1.1.0.250"),sQuery(id+"F0.wireOp",EDGE,"E1.1.0.251"),sQuery(id+"F0.wireOp",EDGE,"E1.1.0.253"),sQuery(id+"F0.wireOp",EDGE,"E1.1.0.257"),sQuery(id+"F0.wireOp",EDGE,"E1.1.0.259"),sQuery(id+"F0.wireOp",EDGE,"E1.1.0.260"),sQuery(id+"F0.wireOp",EDGE,"E1.1.0.264"),sQuery(id+"F0.wireOp",EDGE,"E1.1.0.265"),sQuery(id+"F0.wireOp",EDGE,"E1.1.0.266"),sQuery(id+"F0.wireOp",EDGE,"E1.1.0.269"),sQuery(id+"F0.wireOp",EDGE,"E1.1.0.274"),sQuery(id+"F0.wireOp",EDGE,"E1.1.0.275"),sQuery(id+"F0.wireOp",EDGE,"E1.1.0.276"),sQuery(id+"F0.wireOp",EDGE,"E1.1.0.278"),sQuery(id+"F0.wireOp",EDGE,"E1.1.0.280"),sQuery(id+"F0.wireOp",EDGE,"E1.1.0.284"),sQuery(id+"F0.wireOp",EDGE,"E1.1.0.285"),sQuery(id+"F0.wireOp",EDGE,"E1.1.0.288"),sQuery(id+"F0.wireOp",EDGE,"E1.1.0.289"),sQuery(id+"F0.wireOp",EDGE,"E1.1.0.290"),sQuery(id+"F0.wireOp",EDGE,"E1.1.0.292"),sQuery(id+"F0.wireOp",EDGE,"E1.1.0.293"),sQuery(id+"F0.wireOp",EDGE,"E1.1.0.295"),sQuery(id+"F0.wireOp",EDGE,"E1.1.0.298"),sQuery(id+"F0.wireOp",EDGE,"E1.1.0.299"),sQuery(id+"F0.wireOp",EDGE,"E1.1.0.301"),sQuery(id+"F0.wireOp",EDGE,"E1.1.0.304"),sQuery(id+"F0.wireOp",EDGE,"E1.1.0.305"),sQuery(id+"F0.wireOp",EDGE,"E1.1.0.308"),sQuery(id+"F0.wireOp",EDGE,"E1.1.0.311"),sQuery(id+"F0.wireOp",EDGE,"E1.1.0.312"),sQuery(id+"F0.wireOp",EDGE,"E1.1.0.315"),sQuery(id+"F0.wireOp",EDGE,"E1.1.0.316"),sQuery(id+"F0.wireOp",EDGE,"E1.1.0.317"),sQuery(id+"F0.wireOp",EDGE,"E1.1.0.326"),sQuery(id+"F0.wireOp",EDGE,"E1.1.0.327"),sQuery(id+"F0.wireOp",EDGE,"E1.1.0.328"),sQuery(id+"F0.wireOp",EDGE,"E1.1.0.333"),sQuery(id+"F0.wireOp",EDGE,"E1.1.0.337"),sQuery(id+"F0.wireOp",EDGE,"E1.1.0.340"),sQuery(id+"F0.wireOp",EDGE,"E1.1.0.343"),sQuery(id+"F0.wireOp",EDGE,"E1.1.0.345"),sQuery(id+"F0.wireOp",EDGE,"E1.1.0.349"),sQuery(id+"F0.wireOp",EDGE,"E1.1.0.356"),sQuery(id+"F0.wireOp",EDGE,"E1.1.0.357"),sQuery(id+"F0.wireOp",EDGE,"E1.1.0.363"),sQuery(id+"F0.wireOp",EDGE,"E1.1.0.369"),sQuery(id+"F0.wireOp",EDGE,"E1.1.0.371"),sQuery(id+"F0.wireOp",EDGE,"E1.1.0.374"),sQuery(id+"F0.wireOp",EDGE,"E1.1.0.375"),sQuery(id+"F0.wireOp",EDGE,"E1.1.0.377"),sQuery(id+"F0.wireOp",EDGE,"E1.1.0.382"),sQuery(id+"F0.wireOp",EDGE,"E1.1.0.383"),sQuery(id+"F0.wireOp",EDGE,"E1.1.0.385"),sQuery(id+"F0.wireOp",EDGE,"E1.1.0.386"),sQuery(id+"F0.wireOp",EDGE,"E1.1.0.390"),sQuery(id+"F0.wireOp",EDGE,"E1.1.0.397"),sQuery(id+"F0.wireOp",EDGE,"E1.1.0.399"),sQuery(id+"F0.wireOp",EDGE,"E1.1.0.402"),sQuery(id+"F0.wireOp",EDGE,"E1.1.0.403"),sQuery(id+"F0.wireOp",EDGE,"E1.1.0.410"),sQuery(id+"F0.wireOp",EDGE,"E1.1.0.418"),sQuery(id+"F0.wireOp",EDGE,"E1.1.0.421"),sQuery(id+"F0.wireOp",EDGE,"E1.1.0.423"),sQuery(id+"F0.wireOp",EDGE,"E1.1.0.426"),sQuery(id+"F0.wireOp",EDGE,"E1.1.0.430"),sQuery(id+"F0.wireOp",EDGE,"E1.1.0.432"),sQuery(id+"F0.wireOp",EDGE,"E1.2.0.161"),sQuery(id+"F0.wireOp",EDGE,"E1.2.0.162"),sQuery(id+"F0.wireOp",EDGE,"E1.2.0.163"),sQuery(id+"F0.wireOp",EDGE,"E1.2.0.166"),sQuery(id+"F0.wireOp",EDGE,"E1.2.0.171"),sQuery(id+"F0.wireOp",EDGE,"E1.2.0.173"),sQuery(id+"F0.wireOp",EDGE,"E1.2.0.174"),sQuery(id+"F0.wireOp",EDGE,"E1.2.0.175"),sQuery(id+"F0.wireOp",EDGE,"E1.2.0.176"),sQuery(id+"F0.wireOp",EDGE,"E1.2.0.177"),sQuery(id+"F0.wireOp",EDGE,"E1.2.0.180"),sQuery(id+"F0.wireOp",EDGE,"E1.2.0.185"),sQuery(id+"F0.wireOp",EDGE,"E1.2.0.194"),sQuery(id+"F0.wireOp",EDGE,"E1.2.0.205"),sQuery(id+"F0.wireOp",EDGE,"E1.2.0.215"),sQuery(id+"F0.wireOp",EDGE,"E1.2.0.216"),sQuery(id+"F0.wireOp",EDGE,"E1.2.0.218"),sQuery(id+"F0.wireOp",EDGE,"E1.2.0.222"),sQuery(id+"F0.wireOp",EDGE,"E1.2.0.228"),sQuery(id+"F0.wireOp",EDGE,"E1.2.0.229"),sQuery(id+"F0.wireOp",EDGE,"E1.2.0.230"),sQuery(id+"F0.wireOp",EDGE,"E1.2.0.231"),sQuery(id+"F0.wireOp",EDGE,"E1.2.0.239"),sQuery(id+"F0.wireOp",EDGE,"E1.2.0.240"),sQuery(id+"F0.wireOp",EDGE,"E1.2.0.242"),sQuery(id+"F0.wireOp",EDGE,"E1.2.0.243"),sQuery(id+"F0.wireOp",EDGE,"E1.2.0.244"),sQuery(id+"F0.wireOp",EDGE,"E1.2.0.246"),sQuery(id+"F0.wireOp",EDGE,"E1.2.0.249"),sQuery(id+"F0.wireOp",EDGE,"E1.2.0.250"),sQuery(id+"F0.wireOp",EDGE,"E1.2.0.251"),sQuery(id+"F0.wireOp",EDGE,"E1.2.0.253"),sQuery(id+"F0.wireOp",EDGE,"E1.2.0.257"),sQuery(id+"F0.wireOp",EDGE,"E1.2.0.259"),sQuery(id+"F0.wireOp",EDGE,"E1.2.0.260"),sQuery(id+"F0.wireOp",EDGE,"E1.2.0.264"),sQuery(id+"F0.wireOp",EDGE,"E1.2.0.265"),sQuery(id+"F0.wireOp",EDGE,"E1.2.0.266"),sQuery(id+"F0.wireOp",EDGE,"E1.2.0.269"),sQuery(id+"F0.wireOp",EDGE,"E1.2.0.274"),sQuery(id+"F0.wireOp",EDGE,"E1.2.0.275"),sQuery(id+"F0.wireOp",EDGE,"E1.2.0.276"),sQuery(id+"F0.wireOp",EDGE,"E1.2.0.278"),sQuery(id+"F0.wireOp",EDGE,"E1.2.0.280"),sQuery(id+"F0.wireOp",EDGE,"E1.2.0.284"),sQuery(id+"F0.wireOp",EDGE,"E1.2.0.285"),sQuery(id+"F0.wireOp",EDGE,"E1.2.0.288"),sQuery(id+"F0.wireOp",EDGE,"E1.2.0.289"),sQuery(id+"F0.wireOp",EDGE,"E1.2.0.290"),sQuery(id+"F0.wireOp",EDGE,"E1.2.0.292"),sQuery(id+"F0.wireOp",EDGE,"E1.2.0.293"),sQuery(id+"F0.wireOp",EDGE,"E1.2.0.295"),sQuery(id+"F0.wireOp",EDGE,"E1.2.0.298"),sQuery(id+"F0.wireOp",EDGE,"E1.2.0.299"),sQuery(id+"F0.wireOp",EDGE,"E1.2.0.301"),sQuery(id+"F0.wireOp",EDGE,"E1.2.0.304"),sQuery(id+"F0.wireOp",EDGE,"E1.2.0.305"),sQuery(id+"F0.wireOp",EDGE,"E1.2.0.308"),sQuery(id+"F0.wireOp",EDGE,"E1.2.0.311"),sQuery(id+"F0.wireOp",EDGE,"E1.2.0.312"),sQuery(id+"F0.wireOp",EDGE,"E1.2.0.315"),sQuery(id+"F0.wireOp",EDGE,"E1.2.0.316"),sQuery(id+"F0.wireOp",EDGE,"E1.2.0.317"),sQuery(id+"F0.wireOp",EDGE,"E1.2.0.326"),sQuery(id+"F0.wireOp",EDGE,"E1.2.0.327"),sQuery(id+"F0.wireOp",EDGE,"E1.2.0.328"),sQuery(id+"F0.wireOp",EDGE,"E1.2.0.333"),sQuery(id+"F0.wireOp",EDGE,"E1.2.0.337"),sQuery(id+"F0.wireOp",EDGE,"E1.2.0.340"),sQuery(id+"F0.wireOp",EDGE,"E1.2.0.343"),sQuery(id+"F0.wireOp",EDGE,"E1.2.0.345"),sQuery(id+"F0.wireOp",EDGE,"E1.2.0.349"),sQuery(id+"F0.wireOp",EDGE,"E1.2.0.356"),sQuery(id+"F0.wireOp",EDGE,"E1.2.0.357"),sQuery(id+"F0.wireOp",EDGE,"E1.2.0.363"),sQuery(id+"F0.wireOp",EDGE,"E1.2.0.369"),sQuery(id+"F0.wireOp",EDGE,"E1.2.0.371"),sQuery(id+"F0.wireOp",EDGE,"E1.2.0.374"),sQuery(id+"F0.wireOp",EDGE,"E1.2.0.375"),sQuery(id+"F0.wireOp",EDGE,"E1.2.0.377"),sQuery(id+"F0.wireOp",EDGE,"E1.2.0.382"),sQuery(id+"F0.wireOp",EDGE,"E1.2.0.383"),sQuery(id+"F0.wireOp",EDGE,"E1.2.0.385"),sQuery(id+"F0.wireOp",EDGE,"E1.2.0.386"),sQuery(id+"F0.wireOp",EDGE,"E1.2.0.390"),sQuery(id+"F0.wireOp",EDGE,"E1.2.0.397"),sQuery(id+"F0.wireOp",EDGE,"E1.2.0.399"),sQuery(id+"F0.wireOp",EDGE,"E1.2.0.402"),sQuery(id+"F0.wireOp",EDGE,"E1.2.0.403"),sQuery(id+"F0.wireOp",EDGE,"E1.2.0.410"),sQuery(id+"F0.wireOp",EDGE,"E1.2.0.418"),sQuery(id+"F0.wireOp",EDGE,"E1.2.0.421"),sQuery(id+"F0.wireOp",EDGE,"E1.2.0.423"),sQuery(id+"F0.wireOp",EDGE,"E1.2.0.426"),sQuery(id+"F0.wireOp",EDGE,"E1.2.0.430"),sQuery(id+"F0.wireOp",EDGE,"E1.2.0.432"),sQuery(id+"F0.wireOp",EDGE,"E2.163.3.0"),sQuery(id+"F0.wireOp",EDGE,"E2.166.3.0"),sQuery(id+"F0.wireOp",EDGE,"E2.169.3.0"),sQuery(id+"F0.wireOp",EDGE,"E2.178.3.0"),sQuery(id+"F0.wireOp",EDGE,"E2.193.3.0"),sQuery(id+"F0.wireOp",EDGE,"E2.199.3.0"),sQuery(id+"F0.wireOp",EDGE,"E2.202.3.0"),sQuery(id+"F0.wireOp",EDGE,"E2.205.3.0"),sQuery(id+"F0.wireOp",EDGE,"E2.209.3.0"),sQuery(id+"F0.wireOp",EDGE,"E2.212.3.0"),sQuery(id+"F0.wireOp",EDGE,"E2.221.3.0"),sQuery(id+"F0.wireOp",EDGE,"E2.263.3.0"),sQuery(id+"F0.wireOp",EDGE,"E2.328.3.0"),sQuery(id+"F0.wireOp",EDGE,"E2.332.3.0"),sQuery(id+"F0.wireOp",EDGE,"E2.370.3.0"),sQuery(id+"F0.wireOp",EDGE,"E2.373.3.0"),sQuery(id+"F0.wireOp",EDGE,"E2.379.3.0"),sQuery(id+"F0.wireOp",EDGE,"E2.404.3.0"),sQuery(id+"F0.wireOp",EDGE,"E2.413.3.0"),sQuery(id+"F0.wireOp",EDGE,"E2.416.3.0"),sQuery(id+"F0.wireOp",EDGE,"E2.420.3.0"),sQuery(id+"F0.wireOp",EDGE,"E2.437.3.0"),sQuery(id+"F0.wireOp",EDGE,"E2.440.3.0"),sQuery(id+"F0.wireOp",EDGE,"E2.443.3.0"),sQuery(id+"F0.wireOp",EDGE,"E2.463.3.0"),sQuery(id+"F0.wireOp",EDGE,"E2.469.3.0"),sQuery(id+"F0.wireOp",EDGE,"E2.472.3.0"),sQuery(id+"F0.wireOp",EDGE,"E2.485.3.0"),sQuery(id+"F0.wireOp",EDGE,"E2.502.3.0"),sQuery(id+"F0.wireOp",EDGE,"E2.520.3.0"),sQuery(id+"F0.wireOp",EDGE,"E2.530.3.0"),sQuery(id+"F0.wireOp",EDGE,"E2.554.3.0"),sQuery(id+"F0.wireOp",EDGE,"E2.564.3.0"),sQuery(id+"F0.wireOp",EDGE,"E2.567.3.0"),sQuery(id+"F0.wireOp",EDGE,"E2.571.3.0"),sQuery(id+"F0.wireOp",EDGE,"E2.577.3.0"),sQuery(id+"F0.wireOp",EDGE,"E2.580.3.0"),sQuery(id+"F0.wireOp",EDGE,"E2.586.3.0"),sQuery(id+"F0.wireOp",EDGE,"E2.596.3.0"),sQuery(id+"F0.wireOp",EDGE,"E2.600.3.0"),sQuery(id+"F0.wireOp",EDGE,"E2.607.3.0"),sQuery(id+"F0.wireOp",EDGE,"E2.618.3.0"),sQuery(id+"F0.wireOp",EDGE,"E2.622.3.0"),sQuery(id+"F0.wireOp",EDGE,"E2.645.3.0"),sQuery(id+"F0.wireOp",EDGE,"E2.648.3.0"),sQuery(id+"F0.wireOp",EDGE,"E2.658.3.0"),sQuery(id+"F0.wireOp",EDGE,"E2.665.3.0"),sQuery(id+"F0.wireOp",EDGE,"E2.693.3.0"),sQuery(id+"F0.wireOp",EDGE,"E2.696.3.0"),sQuery(id+"F0.wireOp",EDGE,"E2.699.3.0"),sQuery(id+"F0.wireOp",EDGE,"E2.715.3.0"),sQuery(id+"F0.wireOp",EDGE,"E2.730.3.0"),sQuery(id+"F0.wireOp",EDGE,"E2.742.3.0"),sQuery(id+"F0.wireOp",EDGE,"E2.751.3.0"),sQuery(id+"F0.wireOp",EDGE,"E2.758.3.0"),sQuery(id+"F0.wireOp",EDGE,"E2.773.3.0"),sQuery(id+"F0.wireOp",EDGE,"E2.799.3.0"),sQuery(id+"F0.wireOp",EDGE,"E2.803.3.0"),sQuery(id+"F0.wireOp",EDGE,"E2.825.3.0"),sQuery(id+"F0.wireOp",EDGE,"E2.848.3.0"),sQuery(id+"F0.wireOp",EDGE,"E2.855.3.0"),sQuery(id+"F0.wireOp",EDGE,"E2.866.3.0"),sQuery(id+"F0.wireOp",EDGE,"E2.870.3.0"),sQuery(id+"F0.wireOp",EDGE,"E2.877.3.0"),sQuery(id+"F0.wireOp",EDGE,"E2.894.3.0"),sQuery(id+"F0.wireOp",EDGE,"E2.904.3.0"),sQuery(id+"F0.wireOp",EDGE,"E2.907.3.0"),sQuery(id+"F0.wireOp",EDGE,"E2.922.3.0"),sQuery(id+"F0.wireOp",EDGE,"E2.947.3.0"),sQuery(id+"F0.wireOp",EDGE,"E2.965.3.0"),sQuery(id+"F0.wireOp",EDGE,"E2.992.3.0"),sQuery(id+"F0.wireOp",EDGE,"E2.1020.3.0"),sQuery(id+"F0.wireOp",EDGE,"E2.1038.3.0"),sQuery(id+"F0.wireOp",EDGE,"E2.1049.3.0"),sQuery(id+"F0.wireOp",EDGE,"E2.1063.3.0"),sQuery(id+"F0.wireOp",EDGE,"E2.1070.3.0"),sQuery(id+"F0.wireOp",EDGE,"E3"),sQuery(id+"F0.wireOp",EDGE,"E4"),sQuery(id+"F0.wireOp",EDGE,"E5"),sQuery(id+"F0.wireOp",EDGE,"E6"),sQuery(id+"F0.wireOp",EDGE,"E7"),sQuery(id+"F0.wireOp",EDGE,"E8"),sQuery(id+"F0.wireOp",EDGE,"E9"),sQuery(id+"F0.wireOp",EDGE,"E10"),sQuery(id+"F0.wireOp",EDGE,"E11"),sQuery(id+"F0.wireOp",EDGE,"E12"),sQuery(id+"F0.wireOp",EDGE,"E13"),sQuery(id+"F0.wireOp",EDGE,"E14"),sQuery(id+"F0.wireOp",EDGE,"E15"),sQuery(id+"F0.wireOp",EDGE,"E16"),sQuery(id+"F0.wireOp",EDGE,"E17"),sQuery(id+"F0.wireOp",EDGE,"E18"),sQuery(id+"F0.wireOp",EDGE,"E19"),sQuery(id+"F0.wireOp",EDGE,"E20"),sQuery(id+"F0.wireOp",EDGE,"E21"),sQuery(id+"F0.wireOp",EDGE,"E22"),sQuery(id+"F0.wireOp",EDGE,"E23"),sQuery(id+"F0.wireOp",EDGE,"E24"),sQuery(id+"F0.wireOp",EDGE,"E25"),sQuery(id+"F0.wireOp",EDGE,"E26"),sQuery(id+"F0.wireOp",EDGE,"E27"),sQuery(id+"F0.wireOp",EDGE,"E28"),sQuery(id+"F0.wireOp",EDGE,"E29"),sQuery(id+"F0.wireOp",EDGE,"E30"),sQuery(id+"F0.wireOp",EDGE,"E31"),sQuery(id+"F0.wireOp",EDGE,"E32"),sQuery(id+"F0.wireOp",EDGE,"E33"),sQuery(id+"F0.wireOp",EDGE,"E34"),sQuery(id+"F0.wireOp",EDGE,"E35"),sQuery(id+"F0.wireOp",EDGE,"E36"),sQuery(id+"F0.wireOp",EDGE,"E37"),sQuery(id+"F0.wireOp",EDGE,"E38"),sQuery(id+"F0.wireOp",EDGE,"E39"),sQuery(id+"F0.wireOp",EDGE,"E40"),sQuery(id+"F0.wireOp",EDGE,"E41"),sQuery(id+"F0.wireOp",EDGE,"E42"),sQuery(id+"F0.wireOp",EDGE,"E43"),sQuery(id+"F0.wireOp",EDGE,"E44"),sQuery(id+"F0.wireOp",EDGE,"E45"),sQuery(id+"F0.wireOp",EDGE,"E46"),sQuery(id+"F0.wireOp",EDGE,"E47"),sQuery(id+"F0.wireOp",EDGE,"E48"),sQuery(id+"F0.wireOp",EDGE,"E49"),sQuery(id+"F0.wireOp",EDGE,"E50"),sQuery(id+"F0.wireOp",EDGE,"E51"),sQuery(id+"F0.wireOp",EDGE,"E52.filletArc"),sQuery(id+"F0.wireOp",EDGE,"E53.filletArc"),sQuery(id+"F0.wireOp",EDGE,"E54.filletArc"),sQuery(id+"F0.wireOp",EDGE,"E55.filletArc"),sQuery(id+"F0.wireOp",EDGE,"E56.filletArc"),sQuery(id+"F0.wireOp",EDGE,"E57.filletArc"),sQuery(id+"F0.wireOp",EDGE,"E58.filletArc"),sQuery(id+"F0.wireOp",EDGE,"E59.filletArc"),sQuery(id+"F0.wireOp",EDGE,"E60.trimOffspring"),sQuery(id+"F0.wireOp",EDGE,"E61.filletArc"),sQuery(id+"F0.wireOp",EDGE,"E62.filletArc"),sQuery(id+"F0.wireOp",EDGE,"E63"),sQuery(id+"F0.wireOp",EDGE,"E64"),sQuery(id+"F0.wireOp",EDGE,"E65"),sQuery(id+"F0.wireOp",EDGE,"E66"),sQuery(id+"F0.wireOp",EDGE,"E67"),sQuery(id+"F0.wireOp",EDGE,"E68"),sQuery(id+"F0.wireOp",EDGE,"E69"),sQuery(id+"F0.wireOp",EDGE,"E70"),sQuery(id+"F0.wireOp",EDGE,"E71"),sQuery(id+"F0.wireOp",EDGE,"E72"),sQuery(id+"F0.wireOp",EDGE,"E73.filletArc"),sQuery(id+"F0.wireOp",EDGE,"E74.filletArc"),sQuery(id+"F0.wireOp",EDGE,"E75.filletArc"),sQuery(id+"F0.wireOp",EDGE,"E76.filletArc"),sQuery(id+"F0.wireOp",EDGE,"E77.filletArc"),sQuery(id+"F0.wireOp",EDGE,"E78.filletArc"),sQuery(id+"F0.wireOp",EDGE,"E79.filletArc"),sQuery(id+"F0.wireOp",EDGE,"E80.filletArc"),sQuery(id+"F0.wireOp",EDGE,"E81.filletArc"),sQuery(id+"F0.wireOp",EDGE,"E82.filletArc"),sQuery(id+"F0.wireOp",EDGE,"E83.trimOffspring"),sQuery(id+"F0.wireOp",EDGE,"E84.trimOffspring"),sQuery(id+"F0.wireOp",EDGE,"E85.trimOffspring"),sQuery(id+"F0.wireOp",EDGE,"E86.trimOffspring"),sQuery(id+"F0.wireOp",EDGE,"E87.trimOffspring"),sQuery(id+"F0.wireOp",EDGE,"E88"),sQuery(id+"F0.wireOp",EDGE,"E89"),sQuery(id+"F0.wireOp",EDGE,"E90"),sQuery(id+"F0.wireOp",EDGE,"E91"),sQuery(id+"F0.wireOp",EDGE,"E92"),sQuery(id+"F0.wireOp",EDGE,"E93"),sQuery(id+"F0.wireOp",EDGE,"E94"),sQuery(id+"F0.wireOp",EDGE,"E95"),sQuery(id+"F0.wireOp",EDGE,"E96"),sQuery(id+"F0.wireOp",EDGE,"E97"),sQuery(id+"F0.wireOp",EDGE,"E98"),sQuery(id+"F0.wireOp",EDGE,"E99"),sQuery(id+"F0.wireOp",EDGE,"E100"),sQuery(id+"F0.wireOp",EDGE,"E101"),sQuery(id+"F0.wireOp",EDGE,"E102")])],"isStart":false});
            var sketch = newSketch(context, id + "F6", { "sketchPlane" : qUnion([Q0])});
            skPoint(sketch, "E112.endSnap0", {"position": v(82.1, 29.67) * mm});
            skCircle(sketch, "E113", {"center": v(84.12, 29.5) * mm, "radius": 0.9 * mm});
            skCircle(sketch, "E114", {"center": v(84.12, 29.5) * mm, "radius": 1.5 * mm});
            skSolve(sketch);
        }
        {
            var Q0;
            Q0=makeQuery(id+"F6.imprint","IMPRINT",FACE,{"disambiguationData":[TD([[makeQuery(id+"F6.imprint","IMPRINT",EDGE,{"derivedFrom":sQuery(id+"F6.wireOp",EDGE,"E113")}),-1.0]])]});
            extrude(context, id + "F7", {"entities" : qUnion([Q0]), "operationType" : NewBodyOperationType.ADD, "depth" : 3 * mm, "offsetDistance" : 25 * mm});
        }
    });
